FCSTD DOCUMENT  (FreeCAD 0.18R15684 (Git))
Label: pattern_test_knot4_path
License: All rights reserved
LicenseURL: http://en.wikipedia.org/wiki/All_rights_reserved
objects: Sketcher::SketchObject×244, Part::Feature×243, App::DocumentObjectGroup×2
note: 487 computed .brp shape members not serialized (recipe doc carries the construction recipe); baked Part::Feature solids carry a one-line shape summary decoded from their .brp

FEATURE [Part::Feature] path1691
  shape: bbox 0.3504 x 2.048 x 2e-07 mm, 0 faces, 0 solids (baked)
FEATURE [Part::Feature] path1691001
  shape: bbox 5.227 x 10.07 x 2e-07 mm, 0 faces, 0 solids (baked)
FEATURE [Part::Feature] path1691002
  shape: bbox 3.62 x 11.21 x 2e-07 mm, 0 faces, 0 solids (baked)
FEATURE [Part::Feature] path1691003
  shape: bbox 0.9578 x 6.153 x 2e-07 mm, 0 faces, 0 solids (baked)
FEATURE [Part::Feature] path1691004
  shape: bbox 2.257 x 12.25 x 2e-07 mm, 0 faces, 0 solids (baked)
FEATURE [Part::Feature] path1691005
  shape: bbox 7.072 x 2.907 x 2e-07 mm, 0 faces, 0 solids (baked)
FEATURE [Part::Feature] path1691006
  shape: bbox 2.023 x 11.54 x 2e-07 mm, 0 faces, 0 solids (baked)
FEATURE [Part::Feature] path1691007
  shape: bbox 7.186 x 8.882 x 2e-07 mm, 0 faces, 0 solids (baked)
FEATURE [Part::Feature] path1691008
  shape: bbox 1.074 x 1.58 x 2e-07 mm, 0 faces, 0 solids (baked)
FEATURE [Part::Feature] path1691009
  shape: bbox 0.9879 x 3.768 x 2e-07 mm, 0 faces, 0 solids (baked)
FEATURE [Part::Feature] path1691010
  shape: bbox 4.571 x 8.635 x 2e-07 mm, 0 faces, 0 solids (baked)
FEATURE [Part::Feature] path1691011
  shape: bbox 3.861 x 12.64 x 2e-07 mm, 0 faces, 0 solids (baked)
FEATURE [Part::Feature] path1691012
  shape: bbox 0.7387 x 5.6 x 2e-07 mm, 0 faces, 0 solids (baked)
FEATURE [Part::Feature] path1691013
  shape: bbox 3.309 x 14.24 x 2e-07 mm, 0 faces, 0 solids (baked)
FEATURE [Part::Feature] path1691014
  shape: bbox 6.225 x 2.806 x 2e-07 mm, 0 faces, 0 solids (baked)
FEATURE [Part::Feature] path1691015
  shape: bbox 1.988 x 12.93 x 2e-07 mm, 0 faces, 0 solids (baked)
FEATURE [Part::Feature] path1691016
  shape: bbox 6.325 x 7.842 x 2e-07 mm, 0 faces, 0 solids (baked)
FEATURE [Part::Feature] path1691017
  shape: bbox 1.621 x 2.832 x 2e-07 mm, 0 faces, 0 solids (baked)
FEATURE [Part::Feature] path1691018
  shape: bbox 1.588 x 5.097 x 2e-07 mm, 0 faces, 0 solids (baked)
FEATURE [Part::Feature] path1691019
  shape: bbox 3.926 x 7.273 x 2e-07 mm, 0 faces, 0 solids (baked)
FEATURE [Part::Feature] path1691020
  shape: bbox 4.039 x 13.86 x 2e-07 mm, 0 faces, 0 solids (baked)
FEATURE [Part::Feature] path1691021
  shape: bbox 0.5401 x 5.018 x 2e-07 mm, 0 faces, 0 solids (baked)
FEATURE [Part::Feature] path1691022
  shape: bbox 4.309 x 15.69 x 2e-07 mm, 0 faces, 0 solids (baked)
FEATURE [Part::Feature] path1691023
  shape: bbox 5.323 x 2.698 x 2e-07 mm, 0 faces, 0 solids (baked)
FEATURE [Part::Feature] path1691024
  shape: bbox 1.922 x 3.803 x 2e-07 mm, 0 faces, 0 solids (baked)
FEATURE [Part::Feature] path1691025
  shape: bbox 5.434 x 6.81 x 2e-07 mm, 0 faces, 0 solids (baked)
FEATURE [Part::Feature] path1691026
  shape: bbox 2.605 x 14.03 x 2e-07 mm, 0 faces, 0 solids (baked)
FEATURE [Part::Feature] path1691027
  shape: bbox 1.567 x 1.328 x 2e-07 mm, 0 faces, 0 solids (baked)
FEATURE [Part::Feature] path1691028
  shape: bbox 10.31 x 5.187 x 2e-07 mm, 0 faces, 0 solids (baked)
FEATURE [Part::Feature] path1691029
  shape: bbox 9.647 x 6.66 x 2e-07 mm, 0 faces, 0 solids (baked)
FEATURE [Part::Feature] path1691030
  shape: bbox 3.288 x 5.429 x 2e-07 mm, 0 faces, 0 solids (baked)
FEATURE [Part::Feature] path1691031
  shape: bbox 8.702 x 8.842 x 2e-07 mm, 0 faces, 0 solids (baked)
FEATURE [Part::Feature] path1691032
  shape: bbox 7.276 x 2.368 x 2e-07 mm, 0 faces, 0 solids (baked)
FEATURE [Part::Feature] path1691033
  shape: bbox 6.363 x 9.776 x 2e-07 mm, 0 faces, 0 solids (baked)
FEATURE [Part::Feature] path1691034
  shape: bbox 11.06 x 3.666 x 2e-07 mm, 0 faces, 0 solids (baked)
FEATURE [Part::Feature] path1691035
  shape: bbox 1.798 x 0.5737 x 2e-07 mm, 0 faces, 0 solids (baked)
FEATURE [Part::Feature] path1691036
  shape: bbox 3.13 x 2.234 x 2e-07 mm, 0 faces, 0 solids (baked)
FEATURE [Part::Feature] path1691037
  shape: bbox 8.964 x 4.497 x 2e-07 mm, 0 faces, 0 solids (baked)
FEATURE [Part::Feature] path1691038
  shape: bbox 10.73 x 7.659 x 2e-07 mm, 0 faces, 0 solids (baked)
FEATURE [Part::Feature] path1691039
  shape: bbox 3.078 x 4.836 x 2e-07 mm, 0 faces, 0 solids (baked)
FEATURE [Part::Feature] path1691040
  shape: bbox 10.67 x 9.895 x 2e-07 mm, 0 faces, 0 solids (baked)
FEATURE [Part::Feature] path1691041
  shape: bbox 6.563 x 1.898 x 2e-07 mm, 0 faces, 0 solids (baked)
FEATURE [Part::Feature] path1691042
  shape: bbox 7.893 x 10.29 x 2e-07 mm, 0 faces, 0 solids (baked)
FEATURE [Part::Feature] path1691043
  shape: bbox 9.755 x 3.159 x 2e-07 mm, 0 faces, 0 solids (baked)
FEATURE [Part::Feature] path1691044
  shape: bbox 2.994 x 1.224 x 2e-07 mm, 0 faces, 0 solids (baked)
FEATURE [Part::Feature] path1691045
  shape: bbox 4.409 x 2.869 x 2e-07 mm, 0 faces, 0 solids (baked)
FEATURE [Part::Feature] path1691046
  shape: bbox 7.616 x 3.823 x 2e-07 mm, 0 faces, 0 solids (baked)
FEATURE [Part::Feature] path1691047
  shape: bbox 11.63 x 8.524 x 2e-07 mm, 0 faces, 0 solids (baked)
FEATURE [Part::Feature] path1691048
  shape: bbox 2.836 x 4.236 x 2e-07 mm, 0 faces, 0 solids (baked)
FEATURE [Part::Feature] path1691049
  shape: bbox 12.27 x 10.71 x 2e-07 mm, 0 faces, 0 solids (baked)
FEATURE [Part::Feature] path1691050
  shape: bbox 5.802 x 1.397 x 2e-07 mm, 0 faces, 0 solids (baked)
FEATURE [Part::Feature] path1691051
  shape: bbox 3.83 x 1.807 x 2e-07 mm, 0 faces, 0 solids (baked)
FEATURE [Part::Feature] path1691052
  shape: bbox 8.427 x 2.641 x 2e-07 mm, 0 faces, 0 solids (baked)
FEATURE [Part::Feature] path1691053
  shape: bbox 9.259 x 10.56 x 2e-07 mm, 0 faces, 0 solids (baked)
FEATURE [Part::Feature] path1691054
  shape: bbox 2.053 x 0.14 x 2e-07 mm, 0 faces, 0 solids (baked)
FEATURE [Part::Feature] path1691055
  shape: bbox 10.87 x 3.857 x 2e-07 mm, 0 faces, 0 solids (baked)
FEATURE [Part::Feature] path1691056
  shape: bbox 11.6 x 1.97 x 2e-07 mm, 0 faces, 0 solids (baked)
FEATURE [Part::Feature] path1691057
  shape: bbox 5.851 x 2.085 x 2e-07 mm, 0 faces, 0 solids (baked)
FEATURE [Part::Feature] path1691058
  shape: bbox 12.33 x 2.079 x 2e-07 mm, 0 faces, 0 solids (baked)
FEATURE [Part::Feature] path1691059
  shape: bbox 3.992 x 6.473 x 2e-07 mm, 0 faces, 0 solids (baked)
FEATURE [Part::Feature] path1691060
  shape: bbox 11.13 x 3.76 x 2e-07 mm, 0 faces, 0 solids (baked)
FEATURE [Part::Feature] path1691061
  shape: bbox 9.944 x 5.853 x 2e-07 mm, 0 faces, 0 solids (baked)
FEATURE [Part::Feature] path1691062
  shape: bbox 1.723 x 0.8025 x 2e-07 mm, 0 faces, 0 solids (baked)
FEATURE [Part::Feature] path1691063
  shape: bbox 3.852 x 0.4329 x 2e-07 mm, 0 faces, 0 solids (baked)
FEATURE [Part::Feature] path1691064
  shape: bbox 9.373 x 3.39 x 2e-07 mm, 0 faces, 0 solids (baked)
FEATURE [Part::Feature] path1691065
  shape: bbox 13.06 x 2.031 x 2e-07 mm, 0 faces, 0 solids (baked)
FEATURE [Part::Feature] path1691066
  shape: bbox 5.344 x 1.781 x 2e-07 mm, 0 faces, 0 solids (baked)
FEATURE [Part::Feature] path1691067
  shape: bbox 14.47 x 2.375 x 2e-07 mm, 0 faces, 0 solids (baked)
FEATURE [Part::Feature] path1691068
  shape: bbox 3.759 x 5.66 x 2e-07 mm, 0 faces, 0 solids (baked)
FEATURE [Part::Feature] path1691069
  shape: bbox 12.68 x 3.785 x 2e-07 mm, 0 faces, 0 solids (baked)
FEATURE [Part::Feature] path1691070
  shape: bbox 8.781 x 5.094 x 2e-07 mm, 0 faces, 0 solids (baked)
FEATURE [Part::Feature] path1691071
  shape: bbox 3.044 x 1.138 x 2e-07 mm, 0 faces, 0 solids (baked)
FEATURE [Part::Feature] path1691072
  shape: bbox 5.268 x 0.8515 x 2e-07 mm, 0 faces, 0 solids (baked)
FEATURE [Part::Feature] path1691073
  shape: bbox 7.923 x 2.859 x 2e-07 mm, 0 faces, 0 solids (baked)
FEATURE [Part::Feature] path1691074
  shape: bbox 14.31 x 2.101 x 2e-07 mm, 0 faces, 0 solids (baked)
FEATURE [Part::Feature] path1691075
  shape: bbox 4.805 x 1.488 x 2e-07 mm, 0 faces, 0 solids (baked)
FEATURE [Part::Feature] path1691076
  shape: bbox 16.08 x 3.163 x 2e-07 mm, 0 faces, 0 solids (baked)
FEATURE [Part::Feature] path1691077
  shape: bbox 3.509 x 4.794 x 2e-07 mm, 0 faces, 0 solids (baked)
FEATURE [Part::Feature] path1691078
  shape: bbox 4.05 x 1.277 x 2e-07 mm, 0 faces, 0 solids (baked)
FEATURE [Part::Feature] path1691079
  shape: bbox 7.619 x 4.304 x 2e-07 mm, 0 faces, 0 solids (baked)
FEATURE [Part::Feature] path1691080
  shape: bbox 13.94 x 3.811 x 2e-07 mm, 0 faces, 0 solids (baked)
FEATURE [Part::Feature] path1691081
  shape: bbox 1.559 x 1.332 x 2e-07 mm, 0 faces, 0 solids (baked)
FEATURE [Part::Feature] path1691082
  shape: bbox 6.467 x 9.433 x 2e-07 mm, 0 faces, 0 solids (baked)
FEATURE [Part::Feature] path1691083
  shape: bbox 8.24 x 8.385 x 2e-07 mm, 0 faces, 0 solids (baked)
FEATURE [Part::Feature] path1691084
  shape: bbox 5.856 x 2.384 x 2e-07 mm, 0 faces, 0 solids (baked)
FEATURE [Part::Feature] path1691085
  shape: bbox 10.15 x 7.19 x 2e-07 mm, 0 faces, 0 solids (baked)
FEATURE [Part::Feature] path1691086
  shape: bbox 1.382 x 7.554 x 2e-07 mm, 0 faces, 0 solids (baked)
FEATURE [Part::Feature] path1691087
  shape: bbox 10.65 x 4.733 x 2e-07 mm, 0 faces, 0 solids (baked)
FEATURE [Part::Feature] path1691088
  shape: bbox 4.738 x 10.52 x 2e-07 mm, 0 faces, 0 solids (baked)
FEATURE [Part::Feature] path1691089
  shape: bbox 0.8897 x 1.671 x 2e-07 mm, 0 faces, 0 solids (baked)
FEATURE [Part::Feature] path1691090
  shape: bbox 2.702 x 2.728 x 2e-07 mm, 0 faces, 0 solids (baked)
FEATURE [Part::Feature] path1691091
  shape: bbox 5.533 x 8.223 x 2e-07 mm, 0 faces, 0 solids (baked)
FEATURE [Part::Feature] path1691092
  shape: bbox 9.397 x 9.277 x 2e-07 mm, 0 faces, 0 solids (baked)
FEATURE [Part::Feature] path1691093
  shape: bbox 5.241 x 2.269 x 2e-07 mm, 0 faces, 0 solids (baked)
FEATURE [Part::Feature] path1691094
  shape: bbox 11.46 x 8.969 x 2e-07 mm, 0 faces, 0 solids (baked)
FEATURE [Part::Feature] path1691095
  shape: bbox 1.062 x 6.767 x 2e-07 mm, 0 faces, 0 solids (baked)
FEATURE [Part::Feature] path1691096
  shape: bbox 11.4 x 6.16 x 2e-07 mm, 0 faces, 0 solids (baked)
FEATURE [Part::Feature] path1691097
  shape: bbox 4.178 x 9.267 x 2e-07 mm, 0 faces, 0 solids (baked)
FEATURE [Part::Feature] path1691098
  shape: bbox 1.74 x 2.734 x 2e-07 mm, 0 faces, 0 solids (baked)
FEATURE [Part::Feature] path1691099
  shape: bbox 3.534 x 3.887 x 2e-07 mm, 0 faces, 0 solids (baked)
FEATURE [Part::Feature] path1691100
  shape: bbox 4.691 x 7 x 2e-07 mm, 0 faces, 0 solids (baked)
FEATURE [Part::Feature] path1691101
  shape: bbox 10.39 x 10.01 x 2e-07 mm, 0 faces, 0 solids (baked)
FEATURE [Part::Feature] path1691102
  shape: bbox 4.616 x 2.124 x 2e-07 mm, 0 faces, 0 solids (baked)
FEATURE [Part::Feature] path1691103
  shape: bbox 12.38 x 10.45 x 2e-07 mm, 0 faces, 0 solids (baked)
FEATURE [Part::Feature] path1691104
  shape: bbox 0.7061 x 5.928 x 2e-07 mm, 0 faces, 0 solids (baked)
FEATURE [Part::Feature] path1691105
  shape: bbox 2.457 x 3.454 x 2e-07 mm, 0 faces, 0 solids (baked)
FEATURE [Part::Feature] path1691106
  shape: bbox 3.576 x 7.994 x 2e-07 mm, 0 faces, 0 solids (baked)
FEATURE [Part::Feature] path1691107
  shape: bbox 11.89 x 7.465 x 2e-07 mm, 0 faces, 0 solids (baked)
FEATURE [Part::Feature] path1691108
  shape: bbox 0.4326 x 2 x 2e-07 mm, 0 faces, 0 solids (baked)
FEATURE [Part::Feature] path1691109
  shape: bbox 2.613 x 11.26 x 2e-07 mm, 0 faces, 0 solids (baked)
FEATURE [Part::Feature] path1691110
  shape: bbox 1.547 x 11.7 x 2e-07 mm, 0 faces, 0 solids (baked)
FEATURE [Part::Feature] path1691111
  shape: bbox 3.166 x 5.368 x 2e-07 mm, 0 faces, 0 solids (baked)
FEATURE [Part::Feature] path1691112
  shape: bbox 3.608 x 12.03 x 2e-07 mm, 0 faces, 0 solids (baked)
FEATURE [Part::Feature] path1691113
  shape: bbox 5.654 x 5.019 x 2e-07 mm, 0 faces, 0 solids (baked)
FEATURE [Part::Feature] path1691114
  shape: bbox 5.507 x 10.23 x 2e-07 mm, 0 faces, 0 solids (baked)
FEATURE [Part::Feature] path1691115
  shape: bbox 4.502 x 10.81 x 2e-07 mm, 0 faces, 0 solids (baked)
FEATURE [Part::Feature] path1691116
  shape: bbox 0.4953 x 1.824 x 2e-07 mm, 0 faces, 0 solids (baked)
FEATURE [Part::Feature] path1691117
  shape: bbox 0.6326 x 3.804 x 2e-07 mm, 0 faces, 0 solids (baked)
FEATURE [Part::Feature] path1691118
  shape: bbox 2.308 x 9.728 x 2e-07 mm, 0 faces, 0 solids (baked)
FEATURE [Part::Feature] path1691119
  shape: bbox 1.838 x 13.16 x 2e-07 mm, 0 faces, 0 solids (baked)
FEATURE [Part::Feature] path1691120
  shape: bbox 2.759 x 4.923 x 2e-07 mm, 0 faces, 0 solids (baked)
FEATURE [Part::Feature] path1691121
  shape: bbox 4.121 x 14.25 x 2e-07 mm, 0 faces, 0 solids (baked)
FEATURE [Part::Feature] path1691122
  shape: bbox 4.903 x 4.653 x 2e-07 mm, 0 faces, 0 solids (baked)
FEATURE [Part::Feature] path1691123
  shape: bbox 5.585 x 11.85 x 2e-07 mm, 0 faces, 0 solids (baked)
FEATURE [Part::Feature] path1691124
  shape: bbox 3.857 x 9.555 x 2e-07 mm, 0 faces, 0 solids (baked)
FEATURE [Part::Feature] path1691125
  shape: bbox 0.6126 x 3.18 x 2e-07 mm, 0 faces, 0 solids (baked)
FEATURE [Part::Feature] path1691126
  shape: bbox 0.8239 x 5.237 x 2e-07 mm, 0 faces, 0 solids (baked)
FEATURE [Part::Feature] path1691127
  shape: bbox 1.948 x 8.238 x 2e-07 mm, 0 faces, 0 solids (baked)
FEATURE [Part::Feature] path1691128
  shape: bbox 2.112 x 14.4 x 2e-07 mm, 0 faces, 0 solids (baked)
FEATURE [Part::Feature] path1691129
  shape: bbox 2.359 x 4.445 x 2e-07 mm, 0 faces, 0 solids (baked)
FEATURE [Part::Feature] path1691130
  shape: bbox 4.537 x 15.95 x 2e-07 mm, 0 faces, 0 solids (baked)
FEATURE [Part::Feature] path1691131
  shape: bbox 4.102 x 4.262 x 2e-07 mm, 0 faces, 0 solids (baked)
FEATURE [Part::Feature] path1691132
  shape: bbox 0.6865 x 4.196 x 2e-07 mm, 0 faces, 0 solids (baked)
FEATURE [Part::Feature] path1691133
  shape: bbox 3.179 x 8.287 x 2e-07 mm, 0 faces, 0 solids (baked)
FEATURE [Part::Feature] path1691134
  shape: bbox 5.662 x 13.21 x 2e-07 mm, 0 faces, 0 solids (baked)
FEATURE [Part::Feature] path1691135
  shape: bbox 1.05 x 1.756 x 2e-07 mm, 0 faces, 0 solids (baked)
FEATURE [Part::Feature] path1691136
  shape: bbox 8.272 x 7.856 x 2e-07 mm, 0 faces, 0 solids (baked)
FEATURE [Part::Feature] path1691137
  shape: bbox 6.96 x 9.524 x 2e-07 mm, 0 faces, 0 solids (baked)
FEATURE [Part::Feature] path1691138
  shape: bbox 1.375 x 6.119 x 2e-07 mm, 0 faces, 0 solids (baked)
FEATURE [Part::Feature] path1691139
  shape: bbox 5.496 x 11.16 x 2e-07 mm, 0 faces, 0 solids (baked)
FEATURE [Part::Feature] path1691140
  shape: bbox 7.613 x 1.186 x 2e-07 mm, 0 faces, 0 solids (baked)
FEATURE [Part::Feature] path1691141
  shape: bbox 2.932 x 11.23 x 2e-07 mm, 0 faces, 0 solids (baked)
FEATURE [Part::Feature] path1691142
  shape: bbox 9.689 x 6.196 x 2e-07 mm, 0 faces, 0 solids (baked)
FEATURE [Part::Feature] path1691143
  shape: bbox 1.508 x 1.163 x 2e-07 mm, 0 faces, 0 solids (baked)
FEATURE [Part::Feature] path1691144
  shape: bbox 2.237 x 3.114 x 2e-07 mm, 0 faces, 0 solids (baked)
FEATURE [Part::Feature] path1691145
  shape: bbox 7.24 x 6.674 x 2e-07 mm, 0 faces, 0 solids (baked)
FEATURE [Part::Feature] path1691146
  shape: bbox 7.65 x 10.81 x 2e-07 mm, 0 faces, 0 solids (baked)
FEATURE [Part::Feature] path1691147
  shape: bbox 1.364 x 5.504 x 2e-07 mm, 0 faces, 0 solids (baked)
FEATURE [Part::Feature] path1691148
  shape: bbox 7.043 x 12.73 x 2e-07 mm, 0 faces, 0 solids (baked)
FEATURE [Part::Feature] path1691149
  shape: bbox 6.778 x 1.178 x 2e-07 mm, 0 faces, 0 solids (baked)
FEATURE [Part::Feature] path1691150
  shape: bbox 4.221 x 12.21 x 2e-07 mm, 0 faces, 0 solids (baked)
FEATURE [Part::Feature] path1691151
  shape: bbox 8.532 x 5.472 x 2e-07 mm, 0 faces, 0 solids (baked)
FEATURE [Part::Feature] path1691152
  shape: bbox 2.419 x 2.18 x 2e-07 mm, 0 faces, 0 solids (baked)
FEATURE [Part::Feature] path1691153
  shape: bbox 3.244 x 4.127 x 2e-07 mm, 0 faces, 0 solids (baked)
FEATURE [Part::Feature] path1691154
  shape: bbox 6.18 x 5.581 x 2e-07 mm, 0 faces, 0 solids (baked)
FEATURE [Part::Feature] path1691155
  shape: bbox 8.212 x 11.9 x 2e-07 mm, 0 faces, 0 solids (baked)
FEATURE [Part::Feature] path1691156
  shape: bbox 1.324 x 4.873 x 2e-07 mm, 0 faces, 0 solids (baked)
FEATURE [Part::Feature] path1691157
  shape: bbox 8.367 x 13.8 x 2e-07 mm, 0 faces, 0 solids (baked)
FEATURE [Part::Feature] path1691158
  shape: bbox 5.89 x 1.18 x 2e-07 mm, 0 faces, 0 solids (baked)
FEATURE [Part::Feature] path1691159
  shape: bbox 3.01 x 3.007 x 2e-07 mm, 0 faces, 0 solids (baked)
FEATURE [Part::Feature] path1691160
  shape: bbox 7.35 x 4.767 x 2e-07 mm, 0 faces, 0 solids (baked)
FEATURE [Part::Feature] path1691161
  shape: bbox 5.432 x 12.91 x 2e-07 mm, 0 faces, 0 solids (baked)
FEATURE [Part::Feature] path1691162
  shape: bbox 1.901 x 0.7651 x 2e-07 mm, 0 faces, 0 solids (baked)
FEATURE [Part::Feature] path1691163
  shape: bbox 11.22 x 2.933 x 2e-07 mm, 0 faces, 0 solids (baked)
FEATURE [Part::Feature] path1691164
  shape: bbox 11.48 x 3.19 x 2e-07 mm, 0 faces, 0 solids (baked)
FEATURE [Part::Feature] path1691165
  shape: bbox 4.779 x 4.084 x 2e-07 mm, 0 faces, 0 solids (baked)
FEATURE [Part::Feature] path1691166
  shape: bbox 11.18 x 5.58 x 2e-07 mm, 0 faces, 0 solids (baked)
FEATURE [Part::Feature] path1691167
  shape: bbox 5.988 x 4.615 x 2e-07 mm, 0 faces, 0 solids (baked)
FEATURE [Part::Feature] path1691168
  shape: bbox 9.109 x 7.176 x 2e-07 mm, 0 faces, 0 solids (baked)
FEATURE [Part::Feature] path1691169
  shape: bbox 11.3 x 3.072 x 2e-07 mm, 0 faces, 0 solids (baked)
FEATURE [Part::Feature] path1691170
  shape: bbox 1.882 x 0.1704 x 2e-07 mm, 0 faces, 0 solids (baked)
FEATURE [Part::Feature] path1691171
  shape: bbox 3.668 x 1.129 x 2e-07 mm, 0 faces, 0 solids (baked)
FEATURE [Part::Feature] path1691172
  shape: bbox 9.716 x 2.495 x 2e-07 mm, 0 faces, 0 solids (baked)
FEATURE [Part::Feature] path1691173
  shape: bbox 12.87 x 3.753 x 2e-07 mm, 0 faces, 0 solids (baked)
FEATURE [Part::Feature] path1691174
  shape: bbox 4.405 x 3.594 x 2e-07 mm, 0 faces, 0 solids (baked)
FEATURE [Part::Feature] path1691175
  shape: bbox 13.4 x 6.275 x 2e-07 mm, 0 faces, 0 solids (baked)
FEATURE [Part::Feature] path1691176
  shape: bbox 5.49 x 3.953 x 2e-07 mm, 0 faces, 0 solids (baked)
FEATURE [Part::Feature] path1691177
  shape: bbox 10.74 x 7.298 x 2e-07 mm, 0 faces, 0 solids (baked)
FEATURE [Part::Feature] path1691178
  shape: bbox 9.987 x 2.571 x 2e-07 mm, 0 faces, 0 solids (baked)
FEATURE [Part::Feature] path1691179
  shape: bbox 3.24 x 0.2046 x 2e-07 mm, 0 faces, 0 solids (baked)
FEATURE [Part::Feature] path1691180
  shape: bbox 5.084 x 1.492 x 2e-07 mm, 0 faces, 0 solids (baked)
FEATURE [Part::Feature] path1691181
  shape: bbox 8.235 x 2.06 x 2e-07 mm, 0 faces, 0 solids (baked)
FEATURE [Part::Feature] path1691182
  shape: bbox 14.05 x 4.261 x 2e-07 mm, 0 faces, 0 solids (baked)
FEATURE [Part::Feature] path1691183
  shape: bbox 3.996 x 3.108 x 2e-07 mm, 0 faces, 0 solids (baked)
FEATURE [Part::Feature] path1691184
  shape: bbox 15.13 x 6.831 x 2e-07 mm, 0 faces, 0 solids (baked)
FEATURE [Part::Feature] path1691185
  shape: bbox 4.957 x 3.245 x 2e-07 mm, 0 faces, 0 solids (baked)
FEATURE [Part::Feature] path1691186
  shape: bbox 4.241 x 0.4552 x 2e-07 mm, 0 faces, 0 solids (baked)
FEATURE [Part::Feature] path1691187
  shape: bbox 8.661 x 2.04 x 2e-07 mm, 0 faces, 0 solids (baked)
FEATURE [Part::Feature] path1691188
  shape: bbox 12.13 x 7.421 x 2e-07 mm, 0 faces, 0 solids (baked)
FEATURE [Part::Feature] path1691189
  shape: bbox 1.919 x 0.7232 x 2e-07 mm, 0 faces, 0 solids (baked)
FEATURE [Part::Feature] path1691190
  shape: bbox 9.057 x 6.83 x 2e-07 mm, 0 faces, 0 solids (baked)
FEATURE [Part::Feature] path1691191
  shape: bbox 10.51 x 5.371 x 2e-07 mm, 0 faces, 0 solids (baked)
FEATURE [Part::Feature] path1691192
  shape: bbox 6.218 x 0.5371 x 2e-07 mm, 0 faces, 0 solids (baked)
FEATURE [Part::Feature] path1691193
  shape: bbox 11.86 x 3.621 x 2e-07 mm, 0 faces, 0 solids (baked)
FEATURE [Part::Feature] path1691194
  shape: bbox 1.984 x 7.452 x 2e-07 mm, 0 faces, 0 solids (baked)
FEATURE [Part::Feature] path1691195
  shape: bbox 11.53 x 1.358 x 2e-07 mm, 0 faces, 0 solids (baked)
FEATURE [Part::Feature] path1691196
  shape: bbox 7.633 x 8.579 x 2e-07 mm, 0 faces, 0 solids (baked)
FEATURE [Part::Feature] path1691197
  shape: bbox 1.393 x 1.309 x 2e-07 mm, 0 faces, 0 solids (baked)
FEATURE [Part::Feature] path1691198
  shape: bbox 3.469 x 1.657 x 2e-07 mm, 0 faces, 0 solids (baked)
FEATURE [Part::Feature] path1691199
  shape: bbox 7.733 x 6.015 x 2e-07 mm, 0 faces, 0 solids (baked)
FEATURE [Part::Feature] path1691200
  shape: bbox 11.89 x 5.845 x 2e-07 mm, 0 faces, 0 solids (baked)
FEATURE [Part::Feature] path1691201
  shape: bbox 5.624 x 0.4799 x 2e-07 mm, 0 faces, 0 solids (baked)
FEATURE [Part::Feature] path1691202
  shape: bbox 13.66 x 4.892 x 2e-07 mm, 0 faces, 0 solids (baked)
FEATURE [Part::Feature] path1691203
  shape: bbox 1.795 x 6.598 x 2e-07 mm, 0 faces, 0 solids (baked)
FEATURE [Part::Feature] path1691204
  shape: bbox 12.72 x 2.425 x 2e-07 mm, 0 faces, 0 solids (baked)
FEATURE [Part::Feature] path1691205
  shape: bbox 6.739 x 7.552 x 2e-07 mm, 0 faces, 0 solids (baked)
FEATURE [Part::Feature] path1691206
  shape: bbox 2.544 x 2.047 x 2e-07 mm, 0 faces, 0 solids (baked)
FEATURE [Part::Feature] path1691207
  shape: bbox 4.648 x 2.477 x 2e-07 mm, 0 faces, 0 solids (baked)
FEATURE [Part::Feature] path1691208
  shape: bbox 6.491 x 5.155 x 2e-07 mm, 0 faces, 0 solids (baked)
FEATURE [Part::Feature] path1691209
  shape: bbox 13.06 x 6.22 x 2e-07 mm, 0 faces, 0 solids (baked)
FEATURE [Part::Feature] path1691210
  shape: bbox 5.007 x 0.4917 x 2e-07 mm, 0 faces, 0 solids (baked)
FEATURE [Part::Feature] path1691211
  shape: bbox 14.93 x 6.051 x 2e-07 mm, 0 faces, 0 solids (baked)
FEATURE [Part::Feature] path1691212
  shape: bbox 1.829 x 5.689 x 2e-07 mm, 0 faces, 0 solids (baked)
FEATURE [Part::Feature] path1691213
  shape: bbox 3.455 x 2.499 x 2e-07 mm, 0 faces, 0 solids (baked)
FEATURE [Part::Feature] path1691214
  shape: bbox 5.859 x 6.497 x 2e-07 mm, 0 faces, 0 solids (baked)
FEATURE [Part::Feature] path1691215
  shape: bbox 13.62 x 3.465 x 2e-07 mm, 0 faces, 0 solids (baked)
FEATURE [Part::Feature] path1691216
  shape: bbox 1.064 x 1.757 x 2e-07 mm, 0 faces, 0 solids (baked)
FEATURE [Part::Feature] path1691217
  shape: bbox 4.06 x 10.91 x 2e-07 mm, 0 faces, 0 solids (baked)
FEATURE [Part::Feature] path1691218
  shape: bbox 4.785 x 10.75 x 2e-07 mm, 0 faces, 0 solids (baked)
FEATURE [Part::Feature] path1691219
  shape: bbox 4.839 x 4.086 x 2e-07 mm, 0 faces, 0 solids (baked)
FEATURE [Part::Feature] path1691220
  shape: bbox 7.23 x 10.03 x 2e-07 mm, 0 faces, 0 solids (baked)
FEATURE [Part::Feature] path1691221
  shape: bbox 3.394 x 6.779 x 2e-07 mm, 0 faces, 0 solids (baked)
FEATURE [Part::Feature] path1691222
  shape: bbox 8.619 x 7.822 x 2e-07 mm, 0 faces, 0 solids (baked)
FEATURE [Part::Feature] path1691223
  shape: bbox 2.678 x 11.33 x 2e-07 mm, 0 faces, 0 solids (baked)
FEATURE [Part::Feature] path1691224
  shape: bbox 0.2165 x 1.889 x 2e-07 mm, 0 faces, 0 solids (baked)
FEATURE [Part::Feature] path1691225
  shape: bbox 1.71 x 3.444 x 2e-07 mm, 0 faces, 0 solids (baked)
FEATURE [Part::Feature] path1691226
  shape: bbox 3.504 x 9.461 x 2e-07 mm, 0 faces, 0 solids (baked)
FEATURE [Part::Feature] path1691227
  shape: bbox 5.592 x 12 x 2e-07 mm, 0 faces, 0 solids (baked)
FEATURE [Part::Feature] path1691228
  shape: bbox 4.287 x 3.79 x 2e-07 mm, 0 faces, 0 solids (baked)
FEATURE [Part::Feature] path1691229
  shape: bbox 8.111 x 12.15 x 2e-07 mm, 0 faces, 0 solids (baked)
FEATURE [Part::Feature] path1691230
  shape: bbox 2.828 x 6.167 x 2e-07 mm, 0 faces, 0 solids (baked)
FEATURE [Part::Feature] path1691231
  shape: bbox 8.888 x 9.419 x 2e-07 mm, 0 faces, 0 solids (baked)
FEATURE [Part::Feature] path1691232
  shape: bbox 2.247 x 9.998 x 2e-07 mm, 0 faces, 0 solids (baked)
FEATURE [Part::Feature] path1691233
  shape: bbox 0.632 x 3.198 x 2e-07 mm, 0 faces, 0 solids (baked)
FEATURE [Part::Feature] path1691234
  shape: bbox 2.132 x 4.808 x 2e-07 mm, 0 faces, 0 solids (baked)
FEATURE [Part::Feature] path1691235
  shape: bbox 2.952 x 8.028 x 2e-07 mm, 0 faces, 0 solids (baked)
FEATURE [Part::Feature] path1691236
  shape: bbox 6.302 x 13.05 x 2e-07 mm, 0 faces, 0 solids (baked)
FEATURE [Part::Feature] path1691237
  shape: bbox 3.733 x 3.46 x 2e-07 mm, 0 faces, 0 solids (baked)
FEATURE [Part::Feature] path1691238
  shape: bbox 8.822 x 13.83 x 2e-07 mm, 0 faces, 0 solids (baked)
FEATURE [Part::Feature] path1691239
  shape: bbox 2.226 x 5.512 x 2e-07 mm, 0 faces, 0 solids (baked)
FEATURE [Part::Feature] path1691240
  shape: bbox 1.056 x 4.14 x 2e-07 mm, 0 faces, 0 solids (baked)
FEATURE [Part::Feature] path1691241
  shape: bbox 1.813 x 8.651 x 2e-07 mm, 0 faces, 0 solids (baked)
FEATURE [Part::Feature] path1691242
  shape: bbox 9.06 x 10.82 x 2e-07 mm, 0 faces, 0 solids (baked)
FEATURE [Sketcher::SketchObject] Sketch
  sketch-geometry (1):
    g0: BSplineCurve PolesCount=4 KnotsCount=2 Degree=3 IsPeriodic=0
FEATURE [Sketcher::SketchObject] Sketch001
  sketch-geometry (1):
    g0: BSplineCurve PolesCount=4 KnotsCount=2 Degree=3 IsPeriodic=0
FEATURE [Sketcher::SketchObject] Sketch002
  sketch-geometry (2):
    g0: BSplineCurve PolesCount=4 KnotsCount=2 Degree=3 IsPeriodic=0
    g1: BSplineCurve PolesCount=4 KnotsCount=2 Degree=3 IsPeriodic=0
  constraints (1):
    c: Coincident(g0,g1)
FEATURE [Sketcher::SketchObject] Sketch003
  sketch-geometry (3):
    g0: BSplineCurve PolesCount=4 KnotsCount=2 Degree=3 IsPeriodic=0
    g1: BSplineCurve PolesCount=4 KnotsCount=2 Degree=3 IsPeriodic=0
    g2: BSplineCurve PolesCount=4 KnotsCount=2 Degree=3 IsPeriodic=0
  constraints (2):
    c: Coincident(g0,g1)
    c: Coincident(g1,g2)
FEATURE [Sketcher::SketchObject] Sketch004
  sketch-geometry (1):
    g0: BSplineCurve PolesCount=4 KnotsCount=2 Degree=3 IsPeriodic=0
FEATURE [Sketcher::SketchObject] Sketch005
  sketch-geometry (3):
    g0: BSplineCurve PolesCount=4 KnotsCount=2 Degree=3 IsPeriodic=0
    g1: BSplineCurve PolesCount=4 KnotsCount=2 Degree=3 IsPeriodic=0
    g2: BSplineCurve PolesCount=4 KnotsCount=2 Degree=3 IsPeriodic=0
  constraints (2):
    c: Coincident(g0,g1)
    c: Coincident(g1,g2)
FEATURE [Sketcher::SketchObject] Sketch006
  sketch-geometry (1):
    g0: BSplineCurve PolesCount=4 KnotsCount=2 Degree=3 IsPeriodic=0
FEATURE [Sketcher::SketchObject] Sketch007
  sketch-geometry (3):
    g0: BSplineCurve PolesCount=4 KnotsCount=2 Degree=3 IsPeriodic=0
    g1: BSplineCurve PolesCount=4 KnotsCount=2 Degree=3 IsPeriodic=0
    g2: BSplineCurve PolesCount=4 KnotsCount=2 Degree=3 IsPeriodic=0
  constraints (2):
    c: Coincident(g0,g1)
    c: Coincident(g1,g2)
FEATURE [Sketcher::SketchObject] Sketch008
  sketch-geometry (3):
    g0: BSplineCurve PolesCount=4 KnotsCount=2 Degree=3 IsPeriodic=0
    g1: BSplineCurve PolesCount=4 KnotsCount=2 Degree=3 IsPeriodic=0
    g2: BSplineCurve PolesCount=4 KnotsCount=2 Degree=3 IsPeriodic=0
  constraints (2):
    c: Coincident(g0,g1)
    c: Coincident(g1,g2)
FEATURE [Sketcher::SketchObject] Sketch009
  sketch-geometry (1):
    g0: BSplineCurve PolesCount=4 KnotsCount=2 Degree=3 IsPeriodic=0
FEATURE [Sketcher::SketchObject] Sketch010
  sketch-geometry (3):
    g0: BSplineCurve PolesCount=4 KnotsCount=2 Degree=3 IsPeriodic=0
    g1: BSplineCurve PolesCount=4 KnotsCount=2 Degree=3 IsPeriodic=0
    g2: BSplineCurve PolesCount=4 KnotsCount=2 Degree=3 IsPeriodic=0
  constraints (2):
    c: Coincident(g0,g1)
    c: Coincident(g1,g2)
FEATURE [Sketcher::SketchObject] Sketch011
  sketch-geometry (1):
    g0: BSplineCurve PolesCount=4 KnotsCount=2 Degree=3 IsPeriodic=0
FEATURE [Sketcher::SketchObject] Sketch012
  sketch-geometry (3):
    g0: BSplineCurve PolesCount=4 KnotsCount=2 Degree=3 IsPeriodic=0
    g1: BSplineCurve PolesCount=4 KnotsCount=2 Degree=3 IsPeriodic=0
    g2: BSplineCurve PolesCount=4 KnotsCount=2 Degree=3 IsPeriodic=0
  constraints (2):
    c: Coincident(g0,g1)
    c: Coincident(g1,g2)
FEATURE [Sketcher::SketchObject] Sketch013
  sketch-geometry (2):
    g0: BSplineCurve PolesCount=4 KnotsCount=2 Degree=3 IsPeriodic=0
    g1: BSplineCurve PolesCount=4 KnotsCount=2 Degree=3 IsPeriodic=0
  constraints (1):
    c: Coincident(g0,g1)
FEATURE [Sketcher::SketchObject] Sketch014
  sketch-geometry (1):
    g0: BSplineCurve PolesCount=4 KnotsCount=2 Degree=3 IsPeriodic=0
FEATURE [Sketcher::SketchObject] Sketch015
  sketch-geometry (2):
    g0: BSplineCurve PolesCount=4 KnotsCount=2 Degree=3 IsPeriodic=0
    g1: BSplineCurve PolesCount=4 KnotsCount=2 Degree=3 IsPeriodic=0
  constraints (1):
    c: Coincident(g0,g1)
FEATURE [Sketcher::SketchObject] Sketch016
  sketch-geometry (1):
    g0: BSplineCurve PolesCount=4 KnotsCount=2 Degree=3 IsPeriodic=0
FEATURE [Sketcher::SketchObject] Sketch017
  sketch-geometry (2):
    g0: BSplineCurve PolesCount=4 KnotsCount=2 Degree=3 IsPeriodic=0
    g1: BSplineCurve PolesCount=4 KnotsCount=2 Degree=3 IsPeriodic=0
  constraints (1):
    c: Coincident(g0,g1)
FEATURE [Sketcher::SketchObject] Sketch018
  sketch-geometry (3):
    g0: BSplineCurve PolesCount=4 KnotsCount=2 Degree=3 IsPeriodic=0
    g1: BSplineCurve PolesCount=4 KnotsCount=2 Degree=3 IsPeriodic=0
    g2: BSplineCurve PolesCount=4 KnotsCount=2 Degree=3 IsPeriodic=0
  constraints (2):
    c: Coincident(g0,g1)
    c: Coincident(g1,g2)
FEATURE [Sketcher::SketchObject] Sketch019
  sketch-geometry (1):
    g0: BSplineCurve PolesCount=4 KnotsCount=2 Degree=3 IsPeriodic=0
FEATURE [Sketcher::SketchObject] Sketch020
  sketch-geometry (3):
    g0: BSplineCurve PolesCount=4 KnotsCount=2 Degree=3 IsPeriodic=0
    g1: BSplineCurve PolesCount=4 KnotsCount=2 Degree=3 IsPeriodic=0
    g2: BSplineCurve PolesCount=4 KnotsCount=2 Degree=3 IsPeriodic=0
  constraints (2):
    c: Coincident(g0,g1)
    c: Coincident(g1,g2)
FEATURE [Sketcher::SketchObject] Sketch021
  sketch-geometry (1):
    g0: BSplineCurve PolesCount=4 KnotsCount=2 Degree=3 IsPeriodic=0
FEATURE [Sketcher::SketchObject] Sketch022
  sketch-geometry (1):
    g0: BSplineCurve PolesCount=4 KnotsCount=2 Degree=3 IsPeriodic=0
FEATURE [Sketcher::SketchObject] Sketch023
  sketch-geometry (1):
    g0: BSplineCurve PolesCount=4 KnotsCount=2 Degree=3 IsPeriodic=0
FEATURE [Sketcher::SketchObject] Sketch024
  sketch-geometry (1):
    g0: BSplineCurve PolesCount=4 KnotsCount=2 Degree=3 IsPeriodic=0
FEATURE [Sketcher::SketchObject] Sketch025
  sketch-geometry (2):
    g0: BSplineCurve PolesCount=4 KnotsCount=2 Degree=3 IsPeriodic=0
    g1: BSplineCurve PolesCount=4 KnotsCount=2 Degree=3 IsPeriodic=0
  constraints (1):
    c: Coincident(g0,g1)
FEATURE [Sketcher::SketchObject] Sketch026
  sketch-geometry (3):
    g0: BSplineCurve PolesCount=4 KnotsCount=2 Degree=3 IsPeriodic=0
    g1: BSplineCurve PolesCount=4 KnotsCount=2 Degree=3 IsPeriodic=0
    g2: BSplineCurve PolesCount=4 KnotsCount=2 Degree=3 IsPeriodic=0
  constraints (2):
    c: Coincident(g0,g1)
    c: Coincident(g1,g2)
FEATURE [Sketcher::SketchObject] Sketch027
  sketch-geometry (3):
    g0: BSplineCurve PolesCount=4 KnotsCount=2 Degree=3 IsPeriodic=0
    g1: BSplineCurve PolesCount=4 KnotsCount=2 Degree=3 IsPeriodic=0
    g2: BSplineCurve PolesCount=4 KnotsCount=2 Degree=3 IsPeriodic=0
  constraints (2):
    c: Coincident(g0,g1)
    c: Coincident(g1,g2)
FEATURE [Sketcher::SketchObject] Sketch028
  sketch-geometry (2):
    g0: BSplineCurve PolesCount=4 KnotsCount=2 Degree=3 IsPeriodic=0
    g1: BSplineCurve PolesCount=4 KnotsCount=2 Degree=3 IsPeriodic=0
  constraints (1):
    c: Coincident(g0,g1)
FEATURE [Sketcher::SketchObject] Sketch029
  sketch-geometry (3):
    g0: BSplineCurve PolesCount=4 KnotsCount=2 Degree=3 IsPeriodic=0
    g1: BSplineCurve PolesCount=4 KnotsCount=2 Degree=3 IsPeriodic=0
    g2: BSplineCurve PolesCount=4 KnotsCount=2 Degree=3 IsPeriodic=0
  constraints (2):
    c: Coincident(g0,g1)
    c: Coincident(g1,g2)
FEATURE [Sketcher::SketchObject] Sketch030
  sketch-geometry (1):
    g0: BSplineCurve PolesCount=4 KnotsCount=2 Degree=3 IsPeriodic=0
FEATURE [Sketcher::SketchObject] Sketch031
  sketch-geometry (3):
    g0: BSplineCurve PolesCount=4 KnotsCount=2 Degree=3 IsPeriodic=0
    g1: BSplineCurve PolesCount=4 KnotsCount=2 Degree=3 IsPeriodic=0
    g2: BSplineCurve PolesCount=4 KnotsCount=2 Degree=3 IsPeriodic=0
  constraints (2):
    c: Coincident(g0,g1)
    c: Coincident(g1,g2)
FEATURE [Sketcher::SketchObject] Sketch032
  sketch-geometry (1):
    g0: BSplineCurve PolesCount=4 KnotsCount=2 Degree=3 IsPeriodic=0
FEATURE [Sketcher::SketchObject] Sketch033
  sketch-geometry (1):
    g0: BSplineCurve PolesCount=4 KnotsCount=2 Degree=3 IsPeriodic=0
FEATURE [Sketcher::SketchObject] Sketch034
  sketch-geometry (2):
    g0: BSplineCurve PolesCount=4 KnotsCount=2 Degree=3 IsPeriodic=0
    g1: BSplineCurve PolesCount=4 KnotsCount=2 Degree=3 IsPeriodic=0
  constraints (1):
    c: Coincident(g0,g1)
FEATURE [Sketcher::SketchObject] Sketch035
  sketch-geometry (1):
    g0: BSplineCurve PolesCount=4 KnotsCount=2 Degree=3 IsPeriodic=0
FEATURE [Sketcher::SketchObject] Sketch036
  sketch-geometry (3):
    g0: BSplineCurve PolesCount=4 KnotsCount=2 Degree=3 IsPeriodic=0
    g1: BSplineCurve PolesCount=4 KnotsCount=2 Degree=3 IsPeriodic=0
    g2: BSplineCurve PolesCount=4 KnotsCount=2 Degree=3 IsPeriodic=0
  constraints (2):
    c: Coincident(g0,g1)
    c: Coincident(g1,g2)
FEATURE [Sketcher::SketchObject] Sketch037
  sketch-geometry (1):
    g0: BSplineCurve PolesCount=4 KnotsCount=2 Degree=3 IsPeriodic=0
FEATURE [Sketcher::SketchObject] Sketch038
  sketch-geometry (3):
    g0: BSplineCurve PolesCount=4 KnotsCount=2 Degree=3 IsPeriodic=0
    g1: BSplineCurve PolesCount=4 KnotsCount=2 Degree=3 IsPeriodic=0
    g2: BSplineCurve PolesCount=4 KnotsCount=2 Degree=3 IsPeriodic=0
  constraints (2):
    c: Coincident(g0,g1)
    c: Coincident(g1,g2)
FEATURE [Sketcher::SketchObject] Sketch039
  sketch-geometry (2):
    g0: BSplineCurve PolesCount=4 KnotsCount=2 Degree=3 IsPeriodic=0
    g1: BSplineCurve PolesCount=4 KnotsCount=2 Degree=3 IsPeriodic=0
  constraints (1):
    c: Coincident(g0,g1)
FEATURE [Sketcher::SketchObject] Sketch040
  sketch-geometry (1):
    g0: BSplineCurve PolesCount=4 KnotsCount=2 Degree=3 IsPeriodic=0
FEATURE [Sketcher::SketchObject] Sketch041
  sketch-geometry (1):
    g0: BSplineCurve PolesCount=4 KnotsCount=2 Degree=3 IsPeriodic=0
FEATURE [Sketcher::SketchObject] Sketch042
  sketch-geometry (2):
    g0: BSplineCurve PolesCount=4 KnotsCount=2 Degree=3 IsPeriodic=0
    g1: BSplineCurve PolesCount=4 KnotsCount=2 Degree=3 IsPeriodic=0
  constraints (1):
    c: Coincident(g0,g1)
FEATURE [Sketcher::SketchObject] Sketch043
  sketch-geometry (3):
    g0: BSplineCurve PolesCount=4 KnotsCount=2 Degree=3 IsPeriodic=0
    g1: BSplineCurve PolesCount=4 KnotsCount=2 Degree=3 IsPeriodic=0
    g2: BSplineCurve PolesCount=4 KnotsCount=2 Degree=3 IsPeriodic=0
  constraints (2):
    c: Coincident(g0,g1)
    c: Coincident(g1,g2)
FEATURE [Sketcher::SketchObject] Sketch044
  sketch-geometry (3):
    g0: BSplineCurve PolesCount=4 KnotsCount=2 Degree=3 IsPeriodic=0
    g1: BSplineCurve PolesCount=4 KnotsCount=2 Degree=3 IsPeriodic=0
    g2: BSplineCurve PolesCount=4 KnotsCount=2 Degree=3 IsPeriodic=0
  constraints (2):
    c: Coincident(g0,g1)
    c: Coincident(g1,g2)
FEATURE [Sketcher::SketchObject] Sketch045
  sketch-geometry (3):
    g0: BSplineCurve PolesCount=4 KnotsCount=2 Degree=3 IsPeriodic=0
    g1: BSplineCurve PolesCount=4 KnotsCount=2 Degree=3 IsPeriodic=0
    g2: BSplineCurve PolesCount=4 KnotsCount=2 Degree=3 IsPeriodic=0
  constraints (2):
    c: Coincident(g0,g1)
    c: Coincident(g1,g2)
FEATURE [Sketcher::SketchObject] Sketch046
  sketch-geometry (2):
    g0: BSplineCurve PolesCount=4 KnotsCount=2 Degree=3 IsPeriodic=0
    g1: BSplineCurve PolesCount=4 KnotsCount=2 Degree=3 IsPeriodic=0
  constraints (1):
    c: Coincident(g0,g1)
FEATURE [Sketcher::SketchObject] Sketch047
  sketch-geometry (1):
    g0: BSplineCurve PolesCount=4 KnotsCount=2 Degree=3 IsPeriodic=0
FEATURE [Sketcher::SketchObject] Sketch048
  sketch-geometry (1):
    g0: BSplineCurve PolesCount=4 KnotsCount=2 Degree=3 IsPeriodic=0
FEATURE [Sketcher::SketchObject] Sketch049
  sketch-geometry (2):
    g0: BSplineCurve PolesCount=4 KnotsCount=2 Degree=3 IsPeriodic=0
    g1: BSplineCurve PolesCount=4 KnotsCount=2 Degree=3 IsPeriodic=0
  constraints (1):
    c: Coincident(g0,g1)
FEATURE [Sketcher::SketchObject] Sketch050
  sketch-geometry (3):
    g0: BSplineCurve PolesCount=4 KnotsCount=2 Degree=3 IsPeriodic=0
    g1: BSplineCurve PolesCount=4 KnotsCount=2 Degree=3 IsPeriodic=0
    g2: BSplineCurve PolesCount=4 KnotsCount=2 Degree=3 IsPeriodic=0
  constraints (2):
    c: Coincident(g0,g1)
    c: Coincident(g1,g2)
FEATURE [Sketcher::SketchObject] Sketch051
  sketch-geometry (1):
    g0: BSplineCurve PolesCount=4 KnotsCount=2 Degree=3 IsPeriodic=0
FEATURE [Sketcher::SketchObject] Sketch052
  sketch-geometry (1):
    g0: BSplineCurve PolesCount=4 KnotsCount=2 Degree=3 IsPeriodic=0
FEATURE [Sketcher::SketchObject] Sketch053
  sketch-geometry (3):
    g0: BSplineCurve PolesCount=4 KnotsCount=2 Degree=3 IsPeriodic=0
    g1: BSplineCurve PolesCount=4 KnotsCount=2 Degree=3 IsPeriodic=0
    g2: BSplineCurve PolesCount=4 KnotsCount=2 Degree=3 IsPeriodic=0
  constraints (2):
    c: Coincident(g0,g1)
    c: Coincident(g1,g2)
FEATURE [Sketcher::SketchObject] Sketch054
  sketch-geometry (1):
    g0: BSplineCurve PolesCount=4 KnotsCount=2 Degree=3 IsPeriodic=0
FEATURE [Sketcher::SketchObject] Sketch055
  sketch-geometry (3):
    g0: BSplineCurve PolesCount=4 KnotsCount=2 Degree=3 IsPeriodic=0
    g1: BSplineCurve PolesCount=4 KnotsCount=2 Degree=3 IsPeriodic=0
    g2: BSplineCurve PolesCount=4 KnotsCount=2 Degree=3 IsPeriodic=0
  constraints (2):
    c: Coincident(g0,g1)
    c: Coincident(g1,g2)
FEATURE [Sketcher::SketchObject] Sketch056
  sketch-geometry (3):
    g0: BSplineCurve PolesCount=4 KnotsCount=2 Degree=3 IsPeriodic=0
    g1: BSplineCurve PolesCount=4 KnotsCount=2 Degree=3 IsPeriodic=0
    g2: BSplineCurve PolesCount=4 KnotsCount=2 Degree=3 IsPeriodic=0
  constraints (2):
    c: Coincident(g0,g1)
    c: Coincident(g1,g2)
FEATURE [Sketcher::SketchObject] Sketch057
  sketch-geometry (1):
    g0: BSplineCurve PolesCount=4 KnotsCount=2 Degree=3 IsPeriodic=0
FEATURE [Sketcher::SketchObject] Sketch058
  sketch-geometry (3):
    g0: BSplineCurve PolesCount=4 KnotsCount=2 Degree=3 IsPeriodic=0
    g1: BSplineCurve PolesCount=4 KnotsCount=2 Degree=3 IsPeriodic=0
    g2: BSplineCurve PolesCount=4 KnotsCount=2 Degree=3 IsPeriodic=0
  constraints (2):
    c: Coincident(g0,g1)
    c: Coincident(g1,g2)
FEATURE [Sketcher::SketchObject] Sketch059
  sketch-geometry (1):
    g0: BSplineCurve PolesCount=4 KnotsCount=2 Degree=3 IsPeriodic=0
FEATURE [Sketcher::SketchObject] Sketch060
  sketch-geometry (2):
    g0: BSplineCurve PolesCount=4 KnotsCount=2 Degree=3 IsPeriodic=0
    g1: BSplineCurve PolesCount=4 KnotsCount=2 Degree=3 IsPeriodic=0
  constraints (1):
    c: Coincident(g0,g1)
FEATURE [Sketcher::SketchObject] Sketch061
  sketch-geometry (2):
    g0: BSplineCurve PolesCount=4 KnotsCount=2 Degree=3 IsPeriodic=0
    g1: BSplineCurve PolesCount=4 KnotsCount=2 Degree=3 IsPeriodic=0
  constraints (1):
    c: Coincident(g0,g1)
FEATURE [Sketcher::SketchObject] Sketch062
  sketch-geometry (1):
    g0: BSplineCurve PolesCount=4 KnotsCount=2 Degree=3 IsPeriodic=0
FEATURE [Sketcher::SketchObject] Sketch063
  sketch-geometry (1):
    g0: BSplineCurve PolesCount=4 KnotsCount=2 Degree=3 IsPeriodic=0
FEATURE [Sketcher::SketchObject] Sketch064
  sketch-geometry (3):
    g0: BSplineCurve PolesCount=4 KnotsCount=2 Degree=3 IsPeriodic=0
    g1: BSplineCurve PolesCount=4 KnotsCount=2 Degree=3 IsPeriodic=0
    g2: BSplineCurve PolesCount=4 KnotsCount=2 Degree=3 IsPeriodic=0
  constraints (2):
    c: Coincident(g0,g1)
    c: Coincident(g1,g2)
FEATURE [Sketcher::SketchObject] Sketch065
  sketch-geometry (3):
    g0: BSplineCurve PolesCount=4 KnotsCount=2 Degree=3 IsPeriodic=0
    g1: BSplineCurve PolesCount=4 KnotsCount=2 Degree=3 IsPeriodic=0
    g2: BSplineCurve PolesCount=4 KnotsCount=2 Degree=3 IsPeriodic=0
  constraints (2):
    c: Coincident(g0,g1)
    c: Coincident(g1,g2)
FEATURE [Sketcher::SketchObject] Sketch066
  sketch-geometry (1):
    g0: BSplineCurve PolesCount=4 KnotsCount=2 Degree=3 IsPeriodic=0
FEATURE [Sketcher::SketchObject] Sketch067
  sketch-geometry (3):
    g0: BSplineCurve PolesCount=4 KnotsCount=2 Degree=3 IsPeriodic=0
    g1: BSplineCurve PolesCount=4 KnotsCount=2 Degree=3 IsPeriodic=0
    g2: BSplineCurve PolesCount=4 KnotsCount=2 Degree=3 IsPeriodic=0
  constraints (2):
    c: Coincident(g0,g1)
    c: Coincident(g1,g2)
FEATURE [Sketcher::SketchObject] Sketch068
  sketch-geometry (3):
    g0: BSplineCurve PolesCount=4 KnotsCount=2 Degree=3 IsPeriodic=0
    g1: BSplineCurve PolesCount=4 KnotsCount=2 Degree=3 IsPeriodic=0
    g2: BSplineCurve PolesCount=4 KnotsCount=2 Degree=3 IsPeriodic=0
  constraints (2):
    c: Coincident(g0,g1)
    c: Coincident(g1,g2)
FEATURE [Sketcher::SketchObject] Sketch069
  sketch-geometry (3):
    g0: BSplineCurve PolesCount=4 KnotsCount=2 Degree=3 IsPeriodic=0
    g1: BSplineCurve PolesCount=4 KnotsCount=2 Degree=3 IsPeriodic=0
    g2: BSplineCurve PolesCount=4 KnotsCount=2 Degree=3 IsPeriodic=0
  constraints (2):
    c: Coincident(g0,g1)
    c: Coincident(g1,g2)
FEATURE [Sketcher::SketchObject] Sketch070
  sketch-geometry (2):
    g0: BSplineCurve PolesCount=4 KnotsCount=2 Degree=3 IsPeriodic=0
    g1: BSplineCurve PolesCount=4 KnotsCount=2 Degree=3 IsPeriodic=0
  constraints (1):
    c: Coincident(g0,g1)
FEATURE [Sketcher::SketchObject] Sketch071
  sketch-geometry (1):
    g0: BSplineCurve PolesCount=4 KnotsCount=2 Degree=3 IsPeriodic=0
FEATURE [Sketcher::SketchObject] Sketch072
  sketch-geometry (1):
    g0: BSplineCurve PolesCount=4 KnotsCount=2 Degree=3 IsPeriodic=0
FEATURE [Sketcher::SketchObject] Sketch073
  sketch-geometry (3):
    g0: BSplineCurve PolesCount=4 KnotsCount=2 Degree=3 IsPeriodic=0
    g1: BSplineCurve PolesCount=4 KnotsCount=2 Degree=3 IsPeriodic=0
    g2: BSplineCurve PolesCount=4 KnotsCount=2 Degree=3 IsPeriodic=0
  constraints (2):
    c: Coincident(g0,g1)
    c: Coincident(g1,g2)
FEATURE [Sketcher::SketchObject] Sketch074
  sketch-geometry (3):
    g0: BSplineCurve PolesCount=4 KnotsCount=2 Degree=3 IsPeriodic=0
    g1: BSplineCurve PolesCount=4 KnotsCount=2 Degree=3 IsPeriodic=0
    g2: BSplineCurve PolesCount=4 KnotsCount=2 Degree=3 IsPeriodic=0
  constraints (2):
    c: Coincident(g0,g1)
    c: Coincident(g1,g2)
FEATURE [Sketcher::SketchObject] Sketch075
  sketch-geometry (1):
    g0: BSplineCurve PolesCount=4 KnotsCount=2 Degree=3 IsPeriodic=0
FEATURE [Sketcher::SketchObject] Sketch076
  sketch-geometry (1):
    g0: BSplineCurve PolesCount=4 KnotsCount=2 Degree=3 IsPeriodic=0
FEATURE [Sketcher::SketchObject] Sketch077
  sketch-geometry (1):
    g0: BSplineCurve PolesCount=4 KnotsCount=2 Degree=3 IsPeriodic=0
FEATURE [Sketcher::SketchObject] Sketch078
  sketch-geometry (1):
    g0: BSplineCurve PolesCount=4 KnotsCount=2 Degree=3 IsPeriodic=0
FEATURE [Sketcher::SketchObject] Sketch079
  sketch-geometry (2):
    g0: BSplineCurve PolesCount=4 KnotsCount=2 Degree=3 IsPeriodic=0
    g1: BSplineCurve PolesCount=4 KnotsCount=2 Degree=3 IsPeriodic=0
  constraints (1):
    c: Coincident(g0,g1)
FEATURE [Sketcher::SketchObject] Sketch080
  sketch-geometry (3):
    g0: BSplineCurve PolesCount=4 KnotsCount=2 Degree=3 IsPeriodic=0
    g1: BSplineCurve PolesCount=4 KnotsCount=2 Degree=3 IsPeriodic=0
    g2: BSplineCurve PolesCount=4 KnotsCount=2 Degree=3 IsPeriodic=0
  constraints (2):
    c: Coincident(g0,g1)
    c: Coincident(g1,g2)
FEATURE [Sketcher::SketchObject] Sketch081
  sketch-geometry (1):
    g0: BSplineCurve PolesCount=4 KnotsCount=2 Degree=3 IsPeriodic=0
FEATURE [Sketcher::SketchObject] Sketch082
  sketch-geometry (2):
    g0: BSplineCurve PolesCount=4 KnotsCount=2 Degree=3 IsPeriodic=0
    g1: BSplineCurve PolesCount=4 KnotsCount=2 Degree=3 IsPeriodic=0
  constraints (1):
    c: Coincident(g0,g1)
FEATURE [Sketcher::SketchObject] Sketch083
  sketch-geometry (3):
    g0: BSplineCurve PolesCount=4 KnotsCount=2 Degree=3 IsPeriodic=0
    g1: BSplineCurve PolesCount=4 KnotsCount=2 Degree=3 IsPeriodic=0
    g2: BSplineCurve PolesCount=4 KnotsCount=2 Degree=3 IsPeriodic=0
  constraints (2):
    c: Coincident(g0,g1)
    c: Coincident(g1,g2)
FEATURE [Sketcher::SketchObject] Sketch084
  sketch-geometry (3):
    g0: BSplineCurve PolesCount=4 KnotsCount=2 Degree=3 IsPeriodic=0
    g1: BSplineCurve PolesCount=4 KnotsCount=2 Degree=3 IsPeriodic=0
    g2: BSplineCurve PolesCount=4 KnotsCount=2 Degree=3 IsPeriodic=0
  constraints (2):
    c: Coincident(g0,g1)
    c: Coincident(g1,g2)
FEATURE [Sketcher::SketchObject] Sketch085
  sketch-geometry (3):
    g0: BSplineCurve PolesCount=4 KnotsCount=2 Degree=3 IsPeriodic=0
    g1: BSplineCurve PolesCount=4 KnotsCount=2 Degree=3 IsPeriodic=0
    g2: BSplineCurve PolesCount=4 KnotsCount=2 Degree=3 IsPeriodic=0
  constraints (2):
    c: Coincident(g0,g1)
    c: Coincident(g1,g2)
FEATURE [Sketcher::SketchObject] Sketch086
  sketch-geometry (1):
    g0: BSplineCurve PolesCount=4 KnotsCount=2 Degree=3 IsPeriodic=0
FEATURE [Sketcher::SketchObject] Sketch087
  sketch-geometry (3):
    g0: BSplineCurve PolesCount=4 KnotsCount=2 Degree=3 IsPeriodic=0
    g1: BSplineCurve PolesCount=4 KnotsCount=2 Degree=3 IsPeriodic=0
    g2: BSplineCurve PolesCount=4 KnotsCount=2 Degree=3 IsPeriodic=0
  constraints (2):
    c: Coincident(g0,g1)
    c: Coincident(g1,g2)
FEATURE [Sketcher::SketchObject] Sketch088
  sketch-geometry (2):
    g0: BSplineCurve PolesCount=4 KnotsCount=2 Degree=3 IsPeriodic=0
    g1: BSplineCurve PolesCount=4 KnotsCount=2 Degree=3 IsPeriodic=0
  constraints (1):
    c: Coincident(g0,g1)
FEATURE [Sketcher::SketchObject] Sketch089
  sketch-geometry (1):
    g0: BSplineCurve PolesCount=4 KnotsCount=2 Degree=3 IsPeriodic=0
FEATURE [Sketcher::SketchObject] Sketch090
  sketch-geometry (1):
    g0: BSplineCurve PolesCount=4 KnotsCount=2 Degree=3 IsPeriodic=0
FEATURE [Sketcher::SketchObject] Sketch091
  sketch-geometry (2):
    g0: BSplineCurve PolesCount=4 KnotsCount=2 Degree=3 IsPeriodic=0
    g1: BSplineCurve PolesCount=4 KnotsCount=2 Degree=3 IsPeriodic=0
  constraints (1):
    c: Coincident(g0,g1)
FEATURE [Sketcher::SketchObject] Sketch092
  sketch-geometry (1):
    g0: BSplineCurve PolesCount=4 KnotsCount=2 Degree=3 IsPeriodic=0
FEATURE [Sketcher::SketchObject] Sketch093
  sketch-geometry (1):
    g0: BSplineCurve PolesCount=4 KnotsCount=2 Degree=3 IsPeriodic=0
FEATURE [Sketcher::SketchObject] Sketch094
  sketch-geometry (3):
    g0: BSplineCurve PolesCount=4 KnotsCount=2 Degree=3 IsPeriodic=0
    g1: BSplineCurve PolesCount=4 KnotsCount=2 Degree=3 IsPeriodic=0
    g2: BSplineCurve PolesCount=4 KnotsCount=2 Degree=3 IsPeriodic=0
  constraints (2):
    c: Coincident(g0,g1)
    c: Coincident(g1,g2)
FEATURE [Sketcher::SketchObject] Sketch095
  sketch-geometry (1):
    g0: BSplineCurve PolesCount=4 KnotsCount=2 Degree=3 IsPeriodic=0
FEATURE [Sketcher::SketchObject] Sketch096
  sketch-geometry (3):
    g0: BSplineCurve PolesCount=4 KnotsCount=2 Degree=3 IsPeriodic=0
    g1: BSplineCurve PolesCount=4 KnotsCount=2 Degree=3 IsPeriodic=0
    g2: BSplineCurve PolesCount=4 KnotsCount=2 Degree=3 IsPeriodic=0
  constraints (2):
    c: Coincident(g0,g1)
    c: Coincident(g1,g2)
FEATURE [Sketcher::SketchObject] Sketch097
  sketch-geometry (2):
    g0: BSplineCurve PolesCount=4 KnotsCount=2 Degree=3 IsPeriodic=0
    g1: BSplineCurve PolesCount=4 KnotsCount=2 Degree=3 IsPeriodic=0
  constraints (1):
    c: Coincident(g0,g1)
FEATURE [Sketcher::SketchObject] Sketch098
  sketch-geometry (1):
    g0: BSplineCurve PolesCount=4 KnotsCount=2 Degree=3 IsPeriodic=0
FEATURE [Sketcher::SketchObject] Sketch099
  sketch-geometry (1):
    g0: BSplineCurve PolesCount=4 KnotsCount=2 Degree=3 IsPeriodic=0
FEATURE [Sketcher::SketchObject] Sketch100
  sketch-geometry (3):
    g0: BSplineCurve PolesCount=4 KnotsCount=2 Degree=3 IsPeriodic=0
    g1: BSplineCurve PolesCount=4 KnotsCount=2 Degree=3 IsPeriodic=0
    g2: BSplineCurve PolesCount=4 KnotsCount=2 Degree=3 IsPeriodic=0
  constraints (2):
    c: Coincident(g0,g1)
    c: Coincident(g1,g2)
FEATURE [Sketcher::SketchObject] Sketch101
  sketch-geometry (3):
    g0: BSplineCurve PolesCount=4 KnotsCount=2 Degree=3 IsPeriodic=0
    g1: BSplineCurve PolesCount=4 KnotsCount=2 Degree=3 IsPeriodic=0
    g2: BSplineCurve PolesCount=4 KnotsCount=2 Degree=3 IsPeriodic=0
  constraints (2):
    c: Coincident(g0,g1)
    c: Coincident(g1,g2)
FEATURE [Sketcher::SketchObject] Sketch102
  sketch-geometry (1):
    g0: BSplineCurve PolesCount=4 KnotsCount=2 Degree=3 IsPeriodic=0
FEATURE [Sketcher::SketchObject] Sketch103
  sketch-geometry (3):
    g0: BSplineCurve PolesCount=4 KnotsCount=2 Degree=3 IsPeriodic=0
    g1: BSplineCurve PolesCount=4 KnotsCount=2 Degree=3 IsPeriodic=0
    g2: BSplineCurve PolesCount=4 KnotsCount=2 Degree=3 IsPeriodic=0
  constraints (2):
    c: Coincident(g0,g1)
    c: Coincident(g1,g2)
FEATURE [Sketcher::SketchObject] Sketch104
  sketch-geometry (1):
    g0: BSplineCurve PolesCount=4 KnotsCount=2 Degree=3 IsPeriodic=0
FEATURE [Sketcher::SketchObject] Sketch105
  sketch-geometry (1):
    g0: BSplineCurve PolesCount=4 KnotsCount=2 Degree=3 IsPeriodic=0
FEATURE [Sketcher::SketchObject] Sketch106
  sketch-geometry (2):
    g0: BSplineCurve PolesCount=4 KnotsCount=2 Degree=3 IsPeriodic=0
    g1: BSplineCurve PolesCount=4 KnotsCount=2 Degree=3 IsPeriodic=0
  constraints (1):
    c: Coincident(g0,g1)
FEATURE [Sketcher::SketchObject] Sketch107
  sketch-geometry (3):
    g0: BSplineCurve PolesCount=4 KnotsCount=2 Degree=3 IsPeriodic=0
    g1: BSplineCurve PolesCount=4 KnotsCount=2 Degree=3 IsPeriodic=0
    g2: BSplineCurve PolesCount=4 KnotsCount=2 Degree=3 IsPeriodic=0
  constraints (2):
    c: Coincident(g0,g1)
    c: Coincident(g1,g2)
FEATURE [Sketcher::SketchObject] Sketch108
  sketch-geometry (2):
    g0: BSplineCurve PolesCount=4 KnotsCount=2 Degree=3 IsPeriodic=0
    g1: BSplineCurve PolesCount=4 KnotsCount=2 Degree=3 IsPeriodic=0
  constraints (1):
    c: Coincident(g0,g1)
FEATURE [Sketcher::SketchObject] Sketch109
  sketch-geometry (3):
    g0: BSplineCurve PolesCount=4 KnotsCount=2 Degree=3 IsPeriodic=0
    g1: BSplineCurve PolesCount=4 KnotsCount=2 Degree=3 IsPeriodic=0
    g2: BSplineCurve PolesCount=4 KnotsCount=2 Degree=3 IsPeriodic=0
  constraints (2):
    c: Coincident(g0,g1)
    c: Coincident(g1,g2)
FEATURE [Sketcher::SketchObject] Sketch110
  sketch-geometry (3):
    g0: BSplineCurve PolesCount=4 KnotsCount=2 Degree=3 IsPeriodic=0
    g1: BSplineCurve PolesCount=4 KnotsCount=2 Degree=3 IsPeriodic=0
    g2: BSplineCurve PolesCount=4 KnotsCount=2 Degree=3 IsPeriodic=0
  constraints (2):
    c: Coincident(g0,g1)
    c: Coincident(g1,g2)
FEATURE [Sketcher::SketchObject] Sketch111
  sketch-geometry (1):
    g0: BSplineCurve PolesCount=4 KnotsCount=2 Degree=3 IsPeriodic=0
FEATURE [Sketcher::SketchObject] Sketch112
  sketch-geometry (4):
    g0: BSplineCurve PolesCount=4 KnotsCount=2 Degree=3 IsPeriodic=0
    g1: BSplineCurve PolesCount=4 KnotsCount=2 Degree=3 IsPeriodic=0
    g2: BSplineCurve PolesCount=4 KnotsCount=2 Degree=3 IsPeriodic=0
    g3: BSplineCurve PolesCount=4 KnotsCount=2 Degree=3 IsPeriodic=0
  constraints (3):
    c: Coincident(g0,g1)
    c: Coincident(g1,g2)
    c: Coincident(g2,g3)
FEATURE [Sketcher::SketchObject] Sketch113
  sketch-geometry (1):
    g0: BSplineCurve PolesCount=4 KnotsCount=2 Degree=3 IsPeriodic=0
FEATURE [Sketcher::SketchObject] Sketch114
  sketch-geometry (3):
    g0: BSplineCurve PolesCount=4 KnotsCount=2 Degree=3 IsPeriodic=0
    g1: BSplineCurve PolesCount=4 KnotsCount=2 Degree=3 IsPeriodic=0
    g2: BSplineCurve PolesCount=4 KnotsCount=2 Degree=3 IsPeriodic=0
  constraints (2):
    c: Coincident(g0,g1)
    c: Coincident(g1,g2)
FEATURE [Sketcher::SketchObject] Sketch115
  sketch-geometry (3):
    g0: BSplineCurve PolesCount=4 KnotsCount=2 Degree=3 IsPeriodic=0
    g1: BSplineCurve PolesCount=4 KnotsCount=2 Degree=3 IsPeriodic=0
    g2: BSplineCurve PolesCount=4 KnotsCount=2 Degree=3 IsPeriodic=0
  constraints (2):
    c: Coincident(g0,g1)
    c: Coincident(g1,g2)
FEATURE [Sketcher::SketchObject] Sketch116
  sketch-geometry (1):
    g0: BSplineCurve PolesCount=4 KnotsCount=2 Degree=3 IsPeriodic=0
FEATURE [Sketcher::SketchObject] Sketch117
  sketch-geometry (1):
    g0: BSplineCurve PolesCount=4 KnotsCount=2 Degree=3 IsPeriodic=0
FEATURE [Sketcher::SketchObject] Sketch118
  sketch-geometry (3):
    g0: BSplineCurve PolesCount=4 KnotsCount=2 Degree=3 IsPeriodic=0
    g1: BSplineCurve PolesCount=4 KnotsCount=2 Degree=3 IsPeriodic=0
    g2: BSplineCurve PolesCount=4 KnotsCount=2 Degree=3 IsPeriodic=0
  constraints (2):
    c: Coincident(g0,g1)
    c: Coincident(g1,g2)
FEATURE [Sketcher::SketchObject] Sketch119
  sketch-geometry (3):
    g0: BSplineCurve PolesCount=4 KnotsCount=2 Degree=3 IsPeriodic=0
    g1: BSplineCurve PolesCount=4 KnotsCount=2 Degree=3 IsPeriodic=0
    g2: BSplineCurve PolesCount=4 KnotsCount=2 Degree=3 IsPeriodic=0
  constraints (2):
    c: Coincident(g0,g1)
    c: Coincident(g1,g2)
FEATURE [Sketcher::SketchObject] Sketch120
  sketch-geometry (1):
    g0: BSplineCurve PolesCount=4 KnotsCount=2 Degree=3 IsPeriodic=0
FEATURE [Sketcher::SketchObject] Sketch121
  sketch-geometry (4):
    g0: BSplineCurve PolesCount=4 KnotsCount=2 Degree=3 IsPeriodic=0
    g1: BSplineCurve PolesCount=4 KnotsCount=2 Degree=3 IsPeriodic=0
    g2: BSplineCurve PolesCount=4 KnotsCount=2 Degree=3 IsPeriodic=0
    g3: BSplineCurve PolesCount=4 KnotsCount=2 Degree=3 IsPeriodic=0
  constraints (3):
    c: Coincident(g0,g1)
    c: Coincident(g1,g2)
    c: Coincident(g2,g3)
FEATURE [Sketcher::SketchObject] Sketch122
  sketch-geometry (1):
    g0: BSplineCurve PolesCount=4 KnotsCount=2 Degree=3 IsPeriodic=0
FEATURE [Sketcher::SketchObject] Sketch123
  sketch-geometry (3):
    g0: BSplineCurve PolesCount=4 KnotsCount=2 Degree=3 IsPeriodic=0
    g1: BSplineCurve PolesCount=4 KnotsCount=2 Degree=3 IsPeriodic=0
    g2: BSplineCurve PolesCount=4 KnotsCount=2 Degree=3 IsPeriodic=0
  constraints (2):
    c: Coincident(g0,g1)
    c: Coincident(g1,g2)
FEATURE [Sketcher::SketchObject] Sketch124
  sketch-geometry (1):
    g0: BSplineCurve PolesCount=4 KnotsCount=2 Degree=3 IsPeriodic=0
FEATURE [Sketcher::SketchObject] Sketch125
  sketch-geometry (1):
    g0: BSplineCurve PolesCount=4 KnotsCount=2 Degree=3 IsPeriodic=0
FEATURE [Sketcher::SketchObject] Sketch126
  sketch-geometry (1):
    g0: BSplineCurve PolesCount=4 KnotsCount=2 Degree=3 IsPeriodic=0
FEATURE [Sketcher::SketchObject] Sketch127
  sketch-geometry (2):
    g0: BSplineCurve PolesCount=4 KnotsCount=2 Degree=3 IsPeriodic=0
    g1: BSplineCurve PolesCount=4 KnotsCount=2 Degree=3 IsPeriodic=0
  constraints (1):
    c: Coincident(g0,g1)
FEATURE [Sketcher::SketchObject] Sketch128
  sketch-geometry (3):
    g0: BSplineCurve PolesCount=4 KnotsCount=2 Degree=3 IsPeriodic=0
    g1: BSplineCurve PolesCount=4 KnotsCount=2 Degree=3 IsPeriodic=0
    g2: BSplineCurve PolesCount=4 KnotsCount=2 Degree=3 IsPeriodic=0
  constraints (2):
    c: Coincident(g0,g1)
    c: Coincident(g1,g2)
FEATURE [Sketcher::SketchObject] Sketch129
  sketch-geometry (1):
    g0: BSplineCurve PolesCount=4 KnotsCount=2 Degree=3 IsPeriodic=0
FEATURE [Sketcher::SketchObject] Sketch130
  sketch-geometry (4):
    g0: BSplineCurve PolesCount=4 KnotsCount=2 Degree=3 IsPeriodic=0
    g1: BSplineCurve PolesCount=4 KnotsCount=2 Degree=3 IsPeriodic=0
    g2: BSplineCurve PolesCount=4 KnotsCount=2 Degree=3 IsPeriodic=0
    g3: BSplineCurve PolesCount=4 KnotsCount=2 Degree=3 IsPeriodic=0
  constraints (3):
    c: Coincident(g0,g1)
    c: Coincident(g1,g2)
    c: Coincident(g2,g3)
FEATURE [Sketcher::SketchObject] Sketch131
  sketch-geometry (1):
    g0: BSplineCurve PolesCount=4 KnotsCount=2 Degree=3 IsPeriodic=0
FEATURE [Sketcher::SketchObject] Sketch132
  sketch-geometry (3):
    g0: BSplineCurve PolesCount=4 KnotsCount=2 Degree=3 IsPeriodic=0
    g1: BSplineCurve PolesCount=4 KnotsCount=2 Degree=3 IsPeriodic=0
    g2: BSplineCurve PolesCount=4 KnotsCount=2 Degree=3 IsPeriodic=0
  constraints (2):
    c: Coincident(g0,g1)
    c: Coincident(g1,g2)
FEATURE [Sketcher::SketchObject] Sketch133
  sketch-geometry (2):
    g0: BSplineCurve PolesCount=4 KnotsCount=2 Degree=3 IsPeriodic=0
    g1: BSplineCurve PolesCount=4 KnotsCount=2 Degree=3 IsPeriodic=0
  constraints (1):
    c: Coincident(g0,g1)
FEATURE [Sketcher::SketchObject] Sketch134
  sketch-geometry (3):
    g0: BSplineCurve PolesCount=4 KnotsCount=2 Degree=3 IsPeriodic=0
    g1: BSplineCurve PolesCount=4 KnotsCount=2 Degree=3 IsPeriodic=0
    g2: BSplineCurve PolesCount=4 KnotsCount=2 Degree=3 IsPeriodic=0
  constraints (2):
    c: Coincident(g0,g1)
    c: Coincident(g1,g2)
FEATURE [Sketcher::SketchObject] Sketch135
  sketch-geometry (1):
    g0: BSplineCurve PolesCount=4 KnotsCount=2 Degree=3 IsPeriodic=0
FEATURE [Sketcher::SketchObject] Sketch136
  sketch-geometry (2):
    g0: BSplineCurve PolesCount=4 KnotsCount=2 Degree=3 IsPeriodic=0
    g1: BSplineCurve PolesCount=4 KnotsCount=2 Degree=3 IsPeriodic=0
  constraints (1):
    c: Coincident(g0,g1)
FEATURE [Sketcher::SketchObject] Sketch137
  sketch-geometry (3):
    g0: BSplineCurve PolesCount=4 KnotsCount=2 Degree=3 IsPeriodic=0
    g1: BSplineCurve PolesCount=4 KnotsCount=2 Degree=3 IsPeriodic=0
    g2: BSplineCurve PolesCount=4 KnotsCount=2 Degree=3 IsPeriodic=0
  constraints (2):
    c: Coincident(g0,g1)
    c: Coincident(g1,g2)
FEATURE [Sketcher::SketchObject] Sketch138
  sketch-geometry (1):
    g0: BSplineCurve PolesCount=4 KnotsCount=2 Degree=3 IsPeriodic=0
FEATURE [Sketcher::SketchObject] Sketch139
  sketch-geometry (3):
    g0: BSplineCurve PolesCount=4 KnotsCount=2 Degree=3 IsPeriodic=0
    g1: BSplineCurve PolesCount=4 KnotsCount=2 Degree=3 IsPeriodic=0
    g2: BSplineCurve PolesCount=4 KnotsCount=2 Degree=3 IsPeriodic=0
  constraints (2):
    c: Coincident(g0,g1)
    c: Coincident(g1,g2)
FEATURE [Sketcher::SketchObject] Sketch140
  sketch-geometry (1):
    g0: BSplineCurve PolesCount=4 KnotsCount=2 Degree=3 IsPeriodic=0
FEATURE [Sketcher::SketchObject] Sketch141
  sketch-geometry (3):
    g0: BSplineCurve PolesCount=4 KnotsCount=2 Degree=3 IsPeriodic=0
    g1: BSplineCurve PolesCount=4 KnotsCount=2 Degree=3 IsPeriodic=0
    g2: BSplineCurve PolesCount=4 KnotsCount=2 Degree=3 IsPeriodic=0
  constraints (2):
    c: Coincident(g0,g1)
    c: Coincident(g1,g2)
FEATURE [Sketcher::SketchObject] Sketch142
  sketch-geometry (2):
    g0: BSplineCurve PolesCount=4 KnotsCount=2 Degree=3 IsPeriodic=0
    g1: BSplineCurve PolesCount=4 KnotsCount=2 Degree=3 IsPeriodic=0
  constraints (1):
    c: Coincident(g0,g1)
FEATURE [Sketcher::SketchObject] Sketch143
  sketch-geometry (1):
    g0: BSplineCurve PolesCount=4 KnotsCount=2 Degree=3 IsPeriodic=0
FEATURE [Sketcher::SketchObject] Sketch144
  sketch-geometry (1):
    g0: BSplineCurve PolesCount=4 KnotsCount=2 Degree=3 IsPeriodic=0
FEATURE [Sketcher::SketchObject] Sketch145
  sketch-geometry (1):
    g0: BSplineCurve PolesCount=4 KnotsCount=2 Degree=3 IsPeriodic=0
FEATURE [Sketcher::SketchObject] Sketch146
  sketch-geometry (3):
    g0: BSplineCurve PolesCount=4 KnotsCount=2 Degree=3 IsPeriodic=0
    g1: BSplineCurve PolesCount=4 KnotsCount=2 Degree=3 IsPeriodic=0
    g2: BSplineCurve PolesCount=4 KnotsCount=2 Degree=3 IsPeriodic=0
  constraints (2):
    c: Coincident(g0,g1)
    c: Coincident(g1,g2)
FEATURE [Sketcher::SketchObject] Sketch147
  sketch-geometry (1):
    g0: BSplineCurve PolesCount=4 KnotsCount=2 Degree=3 IsPeriodic=0
FEATURE [Sketcher::SketchObject] Sketch148
  sketch-geometry (3):
    g0: BSplineCurve PolesCount=4 KnotsCount=2 Degree=3 IsPeriodic=0
    g1: BSplineCurve PolesCount=4 KnotsCount=2 Degree=3 IsPeriodic=0
    g2: BSplineCurve PolesCount=4 KnotsCount=2 Degree=3 IsPeriodic=0
  constraints (2):
    c: Coincident(g0,g1)
    c: Coincident(g1,g2)
FEATURE [Sketcher::SketchObject] Sketch149
  sketch-geometry (1):
    g0: BSplineCurve PolesCount=4 KnotsCount=2 Degree=3 IsPeriodic=0
FEATURE [Sketcher::SketchObject] Sketch150
  sketch-geometry (3):
    g0: BSplineCurve PolesCount=4 KnotsCount=2 Degree=3 IsPeriodic=0
    g1: BSplineCurve PolesCount=4 KnotsCount=2 Degree=3 IsPeriodic=0
    g2: BSplineCurve PolesCount=4 KnotsCount=2 Degree=3 IsPeriodic=0
  constraints (2):
    c: Coincident(g0,g1)
    c: Coincident(g1,g2)
FEATURE [Sketcher::SketchObject] Sketch151
  sketch-geometry (2):
    g0: BSplineCurve PolesCount=4 KnotsCount=2 Degree=3 IsPeriodic=0
    g1: BSplineCurve PolesCount=4 KnotsCount=2 Degree=3 IsPeriodic=0
  constraints (1):
    c: Coincident(g0,g1)
FEATURE [Sketcher::SketchObject] Sketch152
  sketch-geometry (1):
    g0: BSplineCurve PolesCount=4 KnotsCount=2 Degree=3 IsPeriodic=0
FEATURE [Sketcher::SketchObject] Sketch153
  sketch-geometry (2):
    g0: BSplineCurve PolesCount=4 KnotsCount=2 Degree=3 IsPeriodic=0
    g1: BSplineCurve PolesCount=4 KnotsCount=2 Degree=3 IsPeriodic=0
  constraints (1):
    c: Coincident(g0,g1)
FEATURE [Sketcher::SketchObject] Sketch154
  sketch-geometry (2):
    g0: BSplineCurve PolesCount=4 KnotsCount=2 Degree=3 IsPeriodic=0
    g1: BSplineCurve PolesCount=4 KnotsCount=2 Degree=3 IsPeriodic=0
  constraints (1):
    c: Coincident(g0,g1)
FEATURE [Sketcher::SketchObject] Sketch155
  sketch-geometry (3):
    g0: BSplineCurve PolesCount=4 KnotsCount=2 Degree=3 IsPeriodic=0
    g1: BSplineCurve PolesCount=4 KnotsCount=2 Degree=3 IsPeriodic=0
    g2: BSplineCurve PolesCount=4 KnotsCount=2 Degree=3 IsPeriodic=0
  constraints (2):
    c: Coincident(g0,g1)
    c: Coincident(g1,g2)
FEATURE [Sketcher::SketchObject] Sketch156
  sketch-geometry (1):
    g0: BSplineCurve PolesCount=4 KnotsCount=2 Degree=3 IsPeriodic=0
FEATURE [Sketcher::SketchObject] Sketch157
  sketch-geometry (3):
    g0: BSplineCurve PolesCount=4 KnotsCount=2 Degree=3 IsPeriodic=0
    g1: BSplineCurve PolesCount=4 KnotsCount=2 Degree=3 IsPeriodic=0
    g2: BSplineCurve PolesCount=4 KnotsCount=2 Degree=3 IsPeriodic=0
  constraints (2):
    c: Coincident(g0,g1)
    c: Coincident(g1,g2)
FEATURE [Sketcher::SketchObject] Sketch158
  sketch-geometry (1):
    g0: BSplineCurve PolesCount=4 KnotsCount=2 Degree=3 IsPeriodic=0
FEATURE [Sketcher::SketchObject] Sketch159
  sketch-geometry (1):
    g0: BSplineCurve PolesCount=4 KnotsCount=2 Degree=3 IsPeriodic=0
FEATURE [Sketcher::SketchObject] Sketch160
  sketch-geometry (2):
    g0: BSplineCurve PolesCount=4 KnotsCount=2 Degree=3 IsPeriodic=0
    g1: BSplineCurve PolesCount=4 KnotsCount=2 Degree=3 IsPeriodic=0
  constraints (1):
    c: Coincident(g0,g1)
FEATURE [Sketcher::SketchObject] Sketch161
  sketch-geometry (1):
    g0: BSplineCurve PolesCount=4 KnotsCount=2 Degree=3 IsPeriodic=0
FEATURE [Sketcher::SketchObject] Sketch162
  sketch-geometry (3):
    g0: BSplineCurve PolesCount=4 KnotsCount=2 Degree=3 IsPeriodic=0
    g1: BSplineCurve PolesCount=4 KnotsCount=2 Degree=3 IsPeriodic=0
    g2: BSplineCurve PolesCount=4 KnotsCount=2 Degree=3 IsPeriodic=0
  constraints (2):
    c: Coincident(g0,g1)
    c: Coincident(g1,g2)
FEATURE [Sketcher::SketchObject] Sketch163
  sketch-geometry (3):
    g0: BSplineCurve PolesCount=4 KnotsCount=2 Degree=3 IsPeriodic=0
    g1: BSplineCurve PolesCount=4 KnotsCount=2 Degree=3 IsPeriodic=0
    g2: BSplineCurve PolesCount=4 KnotsCount=2 Degree=3 IsPeriodic=0
  constraints (2):
    c: Coincident(g0,g1)
    c: Coincident(g1,g2)
FEATURE [Sketcher::SketchObject] Sketch164
  sketch-geometry (1):
    g0: BSplineCurve PolesCount=4 KnotsCount=2 Degree=3 IsPeriodic=0
FEATURE [Sketcher::SketchObject] Sketch165
  sketch-geometry (1):
    g0: BSplineCurve PolesCount=4 KnotsCount=2 Degree=3 IsPeriodic=0
FEATURE [Sketcher::SketchObject] Sketch166
  sketch-geometry (2):
    g0: BSplineCurve PolesCount=4 KnotsCount=2 Degree=3 IsPeriodic=0
    g1: BSplineCurve PolesCount=4 KnotsCount=2 Degree=3 IsPeriodic=0
  constraints (1):
    c: Coincident(g0,g1)
FEATURE [Sketcher::SketchObject] Sketch167
  sketch-geometry (3):
    g0: BSplineCurve PolesCount=4 KnotsCount=2 Degree=3 IsPeriodic=0
    g1: BSplineCurve PolesCount=4 KnotsCount=2 Degree=3 IsPeriodic=0
    g2: BSplineCurve PolesCount=4 KnotsCount=2 Degree=3 IsPeriodic=0
  constraints (2):
    c: Coincident(g0,g1)
    c: Coincident(g1,g2)
FEATURE [Sketcher::SketchObject] Sketch168
  sketch-geometry (1):
    g0: BSplineCurve PolesCount=4 KnotsCount=2 Degree=3 IsPeriodic=0
FEATURE [Sketcher::SketchObject] Sketch169
  sketch-geometry (3):
    g0: BSplineCurve PolesCount=4 KnotsCount=2 Degree=3 IsPeriodic=0
    g1: BSplineCurve PolesCount=4 KnotsCount=2 Degree=3 IsPeriodic=0
    g2: BSplineCurve PolesCount=4 KnotsCount=2 Degree=3 IsPeriodic=0
  constraints (2):
    c: Coincident(g0,g1)
    c: Coincident(g1,g2)
FEATURE [Sketcher::SketchObject] Sketch170
  sketch-geometry (1):
    g0: BSplineCurve PolesCount=4 KnotsCount=2 Degree=3 IsPeriodic=0
FEATURE [Sketcher::SketchObject] Sketch171
  sketch-geometry (2):
    g0: BSplineCurve PolesCount=4 KnotsCount=2 Degree=3 IsPeriodic=0
    g1: BSplineCurve PolesCount=4 KnotsCount=2 Degree=3 IsPeriodic=0
  constraints (1):
    c: Coincident(g0,g1)
FEATURE [Sketcher::SketchObject] Sketch172
  sketch-geometry (3):
    g0: BSplineCurve PolesCount=4 KnotsCount=2 Degree=3 IsPeriodic=0
    g1: BSplineCurve PolesCount=4 KnotsCount=2 Degree=3 IsPeriodic=0
    g2: BSplineCurve PolesCount=4 KnotsCount=2 Degree=3 IsPeriodic=0
  constraints (2):
    c: Coincident(g0,g1)
    c: Coincident(g1,g2)
FEATURE [Sketcher::SketchObject] Sketch173
  sketch-geometry (1):
    g0: BSplineCurve PolesCount=4 KnotsCount=2 Degree=3 IsPeriodic=0
FEATURE [Sketcher::SketchObject] Sketch174
  sketch-geometry (3):
    g0: BSplineCurve PolesCount=4 KnotsCount=2 Degree=3 IsPeriodic=0
    g1: BSplineCurve PolesCount=4 KnotsCount=2 Degree=3 IsPeriodic=0
    g2: BSplineCurve PolesCount=4 KnotsCount=2 Degree=3 IsPeriodic=0
  constraints (2):
    c: Coincident(g0,g1)
    c: Coincident(g1,g2)
FEATURE [Sketcher::SketchObject] Sketch175
  sketch-geometry (1):
    g0: BSplineCurve PolesCount=4 KnotsCount=2 Degree=3 IsPeriodic=0
FEATURE [Sketcher::SketchObject] Sketch176
  sketch-geometry (1):
    g0: BSplineCurve PolesCount=4 KnotsCount=2 Degree=3 IsPeriodic=0
FEATURE [Sketcher::SketchObject] Sketch177
  sketch-geometry (3):
    g0: BSplineCurve PolesCount=4 KnotsCount=2 Degree=3 IsPeriodic=0
    g1: BSplineCurve PolesCount=4 KnotsCount=2 Degree=3 IsPeriodic=0
    g2: BSplineCurve PolesCount=4 KnotsCount=2 Degree=3 IsPeriodic=0
  constraints (2):
    c: Coincident(g0,g1)
    c: Coincident(g1,g2)
FEATURE [Sketcher::SketchObject] Sketch178
  sketch-geometry (3):
    g0: BSplineCurve PolesCount=4 KnotsCount=2 Degree=3 IsPeriodic=0
    g1: BSplineCurve PolesCount=4 KnotsCount=2 Degree=3 IsPeriodic=0
    g2: BSplineCurve PolesCount=4 KnotsCount=2 Degree=3 IsPeriodic=0
  constraints (2):
    c: Coincident(g0,g1)
    c: Coincident(g1,g2)
FEATURE [Sketcher::SketchObject] Sketch179
  sketch-geometry (1):
    g0: BSplineCurve PolesCount=4 KnotsCount=2 Degree=3 IsPeriodic=0
FEATURE [Sketcher::SketchObject] Sketch180
  sketch-geometry (1):
    g0: BSplineCurve PolesCount=4 KnotsCount=2 Degree=3 IsPeriodic=0
FEATURE [Sketcher::SketchObject] Sketch181
  sketch-geometry (2):
    g0: BSplineCurve PolesCount=4 KnotsCount=2 Degree=3 IsPeriodic=0
    g1: BSplineCurve PolesCount=4 KnotsCount=2 Degree=3 IsPeriodic=0
  constraints (1):
    c: Coincident(g0,g1)
FEATURE [Sketcher::SketchObject] Sketch182
  sketch-geometry (3):
    g0: BSplineCurve PolesCount=4 KnotsCount=2 Degree=3 IsPeriodic=0
    g1: BSplineCurve PolesCount=4 KnotsCount=2 Degree=3 IsPeriodic=0
    g2: BSplineCurve PolesCount=4 KnotsCount=2 Degree=3 IsPeriodic=0
  constraints (2):
    c: Coincident(g0,g1)
    c: Coincident(g1,g2)
FEATURE [Sketcher::SketchObject] Sketch183
  sketch-geometry (3):
    g0: BSplineCurve PolesCount=4 KnotsCount=2 Degree=3 IsPeriodic=0
    g1: BSplineCurve PolesCount=4 KnotsCount=2 Degree=3 IsPeriodic=0
    g2: BSplineCurve PolesCount=4 KnotsCount=2 Degree=3 IsPeriodic=0
  constraints (2):
    c: Coincident(g0,g1)
    c: Coincident(g1,g2)
FEATURE [Sketcher::SketchObject] Sketch184
  sketch-geometry (4):
    g0: BSplineCurve PolesCount=4 KnotsCount=2 Degree=3 IsPeriodic=0
    g1: BSplineCurve PolesCount=4 KnotsCount=2 Degree=3 IsPeriodic=0
    g2: BSplineCurve PolesCount=4 KnotsCount=2 Degree=3 IsPeriodic=0
    g3: BSplineCurve PolesCount=4 KnotsCount=2 Degree=3 IsPeriodic=0
  constraints (3):
    c: Coincident(g0,g1)
    c: Coincident(g1,g2)
    c: Coincident(g2,g3)
FEATURE [Sketcher::SketchObject] Sketch185
  sketch-geometry (1):
    g0: BSplineCurve PolesCount=4 KnotsCount=2 Degree=3 IsPeriodic=0
FEATURE [Sketcher::SketchObject] Sketch186
  sketch-geometry (1):
    g0: BSplineCurve PolesCount=4 KnotsCount=2 Degree=3 IsPeriodic=0
FEATURE [Sketcher::SketchObject] Sketch187
  sketch-geometry (3):
    g0: BSplineCurve PolesCount=4 KnotsCount=2 Degree=3 IsPeriodic=0
    g1: BSplineCurve PolesCount=4 KnotsCount=2 Degree=3 IsPeriodic=0
    g2: BSplineCurve PolesCount=4 KnotsCount=2 Degree=3 IsPeriodic=0
  constraints (2):
    c: Coincident(g0,g1)
    c: Coincident(g1,g2)
FEATURE [Sketcher::SketchObject] Sketch188
  sketch-geometry (3):
    g0: BSplineCurve PolesCount=4 KnotsCount=2 Degree=3 IsPeriodic=0
    g1: BSplineCurve PolesCount=4 KnotsCount=2 Degree=3 IsPeriodic=0
    g2: BSplineCurve PolesCount=4 KnotsCount=2 Degree=3 IsPeriodic=0
  constraints (2):
    c: Coincident(g0,g1)
    c: Coincident(g1,g2)
FEATURE [Sketcher::SketchObject] Sketch189
  sketch-geometry (1):
    g0: BSplineCurve PolesCount=4 KnotsCount=2 Degree=3 IsPeriodic=0
FEATURE [Sketcher::SketchObject] Sketch190
  sketch-geometry (2):
    g0: BSplineCurve PolesCount=4 KnotsCount=2 Degree=3 IsPeriodic=0
    g1: BSplineCurve PolesCount=4 KnotsCount=2 Degree=3 IsPeriodic=0
  constraints (1):
    c: Coincident(g0,g1)
FEATURE [Sketcher::SketchObject] Sketch191
  sketch-geometry (1):
    g0: BSplineCurve PolesCount=4 KnotsCount=2 Degree=3 IsPeriodic=0
FEATURE [Sketcher::SketchObject] Sketch192
  sketch-geometry (1):
    g0: BSplineCurve PolesCount=4 KnotsCount=2 Degree=3 IsPeriodic=0
FEATURE [Sketcher::SketchObject] Sketch193
  sketch-geometry (3):
    g0: BSplineCurve PolesCount=4 KnotsCount=2 Degree=3 IsPeriodic=0
    g1: BSplineCurve PolesCount=4 KnotsCount=2 Degree=3 IsPeriodic=0
    g2: BSplineCurve PolesCount=4 KnotsCount=2 Degree=3 IsPeriodic=0
  constraints (2):
    c: Coincident(g0,g1)
    c: Coincident(g1,g2)
FEATURE [Sketcher::SketchObject] Sketch194
  sketch-geometry (1):
    g0: BSplineCurve PolesCount=4 KnotsCount=2 Degree=3 IsPeriodic=0
FEATURE [Sketcher::SketchObject] Sketch195
  sketch-geometry (3):
    g0: BSplineCurve PolesCount=4 KnotsCount=2 Degree=3 IsPeriodic=0
    g1: BSplineCurve PolesCount=4 KnotsCount=2 Degree=3 IsPeriodic=0
    g2: BSplineCurve PolesCount=4 KnotsCount=2 Degree=3 IsPeriodic=0
  constraints (2):
    c: Coincident(g0,g1)
    c: Coincident(g1,g2)
FEATURE [Sketcher::SketchObject] Sketch196
  sketch-geometry (2):
    g0: BSplineCurve PolesCount=4 KnotsCount=2 Degree=3 IsPeriodic=0
    g1: BSplineCurve PolesCount=4 KnotsCount=2 Degree=3 IsPeriodic=0
  constraints (1):
    c: Coincident(g0,g1)
FEATURE [Sketcher::SketchObject] Sketch197
  sketch-geometry (1):
    g0: BSplineCurve PolesCount=4 KnotsCount=2 Degree=3 IsPeriodic=0
FEATURE [Sketcher::SketchObject] Sketch198
  sketch-geometry (1):
    g0: BSplineCurve PolesCount=4 KnotsCount=2 Degree=3 IsPeriodic=0
FEATURE [Sketcher::SketchObject] Sketch199
  sketch-geometry (3):
    g0: BSplineCurve PolesCount=4 KnotsCount=2 Degree=3 IsPeriodic=0
    g1: BSplineCurve PolesCount=4 KnotsCount=2 Degree=3 IsPeriodic=0
    g2: BSplineCurve PolesCount=4 KnotsCount=2 Degree=3 IsPeriodic=0
  constraints (2):
    c: Coincident(g0,g1)
    c: Coincident(g1,g2)
FEATURE [Sketcher::SketchObject] Sketch200
  sketch-geometry (3):
    g0: BSplineCurve PolesCount=4 KnotsCount=2 Degree=3 IsPeriodic=0
    g1: BSplineCurve PolesCount=4 KnotsCount=2 Degree=3 IsPeriodic=0
    g2: BSplineCurve PolesCount=4 KnotsCount=2 Degree=3 IsPeriodic=0
  constraints (2):
    c: Coincident(g0,g1)
    c: Coincident(g1,g2)
FEATURE [Sketcher::SketchObject] Sketch201
  sketch-geometry (1):
    g0: BSplineCurve PolesCount=4 KnotsCount=2 Degree=3 IsPeriodic=0
FEATURE [Sketcher::SketchObject] Sketch202
  sketch-geometry (3):
    g0: BSplineCurve PolesCount=4 KnotsCount=2 Degree=3 IsPeriodic=0
    g1: BSplineCurve PolesCount=4 KnotsCount=2 Degree=3 IsPeriodic=0
    g2: BSplineCurve PolesCount=4 KnotsCount=2 Degree=3 IsPeriodic=0
  constraints (2):
    c: Coincident(g0,g1)
    c: Coincident(g1,g2)
FEATURE [Sketcher::SketchObject] Sketch203
  sketch-geometry (1):
    g0: BSplineCurve PolesCount=4 KnotsCount=2 Degree=3 IsPeriodic=0
FEATURE [Sketcher::SketchObject] Sketch204
  sketch-geometry (3):
    g0: BSplineCurve PolesCount=4 KnotsCount=2 Degree=3 IsPeriodic=0
    g1: BSplineCurve PolesCount=4 KnotsCount=2 Degree=3 IsPeriodic=0
    g2: BSplineCurve PolesCount=4 KnotsCount=2 Degree=3 IsPeriodic=0
  constraints (2):
    c: Coincident(g0,g1)
    c: Coincident(g1,g2)
FEATURE [Sketcher::SketchObject] Sketch205
  sketch-geometry (2):
    g0: BSplineCurve PolesCount=4 KnotsCount=2 Degree=3 IsPeriodic=0
    g1: BSplineCurve PolesCount=4 KnotsCount=2 Degree=3 IsPeriodic=0
  constraints (1):
    c: Coincident(g0,g1)
FEATURE [Sketcher::SketchObject] Sketch206
  sketch-geometry (1):
    g0: BSplineCurve PolesCount=4 KnotsCount=2 Degree=3 IsPeriodic=0
FEATURE [Sketcher::SketchObject] Sketch207
  sketch-geometry (2):
    g0: BSplineCurve PolesCount=4 KnotsCount=2 Degree=3 IsPeriodic=0
    g1: BSplineCurve PolesCount=4 KnotsCount=2 Degree=3 IsPeriodic=0
  constraints (1):
    c: Coincident(g0,g1)
FEATURE [Sketcher::SketchObject] Sketch208
  sketch-geometry (2):
    g0: BSplineCurve PolesCount=4 KnotsCount=2 Degree=3 IsPeriodic=0
    g1: BSplineCurve PolesCount=4 KnotsCount=2 Degree=3 IsPeriodic=0
  constraints (1):
    c: Coincident(g0,g1)
FEATURE [Sketcher::SketchObject] Sketch209
  sketch-geometry (3):
    g0: BSplineCurve PolesCount=4 KnotsCount=2 Degree=3 IsPeriodic=0
    g1: BSplineCurve PolesCount=4 KnotsCount=2 Degree=3 IsPeriodic=0
    g2: BSplineCurve PolesCount=4 KnotsCount=2 Degree=3 IsPeriodic=0
  constraints (2):
    c: Coincident(g0,g1)
    c: Coincident(g1,g2)
FEATURE [Sketcher::SketchObject] Sketch210
  sketch-geometry (1):
    g0: BSplineCurve PolesCount=4 KnotsCount=2 Degree=3 IsPeriodic=0
FEATURE [Sketcher::SketchObject] Sketch211
  sketch-geometry (3):
    g0: BSplineCurve PolesCount=4 KnotsCount=2 Degree=3 IsPeriodic=0
    g1: BSplineCurve PolesCount=4 KnotsCount=2 Degree=3 IsPeriodic=0
    g2: BSplineCurve PolesCount=4 KnotsCount=2 Degree=3 IsPeriodic=0
  constraints (2):
    c: Coincident(g0,g1)
    c: Coincident(g1,g2)
FEATURE [Sketcher::SketchObject] Sketch212
  sketch-geometry (1):
    g0: BSplineCurve PolesCount=4 KnotsCount=2 Degree=3 IsPeriodic=0
FEATURE [Sketcher::SketchObject] Sketch213
  sketch-geometry (1):
    g0: BSplineCurve PolesCount=4 KnotsCount=2 Degree=3 IsPeriodic=0
FEATURE [Sketcher::SketchObject] Sketch214
  sketch-geometry (2):
    g0: BSplineCurve PolesCount=4 KnotsCount=2 Degree=3 IsPeriodic=0
    g1: BSplineCurve PolesCount=4 KnotsCount=2 Degree=3 IsPeriodic=0
  constraints (1):
    c: Coincident(g0,g1)
FEATURE [Sketcher::SketchObject] Sketch215
  sketch-geometry (1):
    g0: BSplineCurve PolesCount=4 KnotsCount=2 Degree=3 IsPeriodic=0
FEATURE [Sketcher::SketchObject] Sketch216
  sketch-geometry (1):
    g0: BSplineCurve PolesCount=4 KnotsCount=2 Degree=3 IsPeriodic=0
FEATURE [Sketcher::SketchObject] Sketch217
  sketch-geometry (2):
    g0: BSplineCurve PolesCount=4 KnotsCount=2 Degree=3 IsPeriodic=0
    g1: BSplineCurve PolesCount=4 KnotsCount=2 Degree=3 IsPeriodic=0
  constraints (1):
    c: Coincident(g0,g1)
FEATURE [Sketcher::SketchObject] Sketch218
  sketch-geometry (3):
    g0: BSplineCurve PolesCount=4 KnotsCount=2 Degree=3 IsPeriodic=0
    g1: BSplineCurve PolesCount=4 KnotsCount=2 Degree=3 IsPeriodic=0
    g2: BSplineCurve PolesCount=4 KnotsCount=2 Degree=3 IsPeriodic=0
  constraints (2):
    c: Coincident(g0,g1)
    c: Coincident(g1,g2)
FEATURE [Sketcher::SketchObject] Sketch219
  sketch-geometry (1):
    g0: BSplineCurve PolesCount=4 KnotsCount=2 Degree=3 IsPeriodic=0
FEATURE [Sketcher::SketchObject] Sketch220
  sketch-geometry (3):
    g0: BSplineCurve PolesCount=4 KnotsCount=2 Degree=3 IsPeriodic=0
    g1: BSplineCurve PolesCount=4 KnotsCount=2 Degree=3 IsPeriodic=0
    g2: BSplineCurve PolesCount=4 KnotsCount=2 Degree=3 IsPeriodic=0
  constraints (2):
    c: Coincident(g0,g1)
    c: Coincident(g1,g2)
FEATURE [Sketcher::SketchObject] Sketch221
  sketch-geometry (1):
    g0: BSplineCurve PolesCount=4 KnotsCount=2 Degree=3 IsPeriodic=0
FEATURE [Sketcher::SketchObject] Sketch222
  sketch-geometry (3):
    g0: BSplineCurve PolesCount=4 KnotsCount=2 Degree=3 IsPeriodic=0
    g1: BSplineCurve PolesCount=4 KnotsCount=2 Degree=3 IsPeriodic=0
    g2: BSplineCurve PolesCount=4 KnotsCount=2 Degree=3 IsPeriodic=0
  constraints (2):
    c: Coincident(g0,g1)
    c: Coincident(g1,g2)
FEATURE [Sketcher::SketchObject] Sketch223
  sketch-geometry (3):
    g0: BSplineCurve PolesCount=4 KnotsCount=2 Degree=3 IsPeriodic=0
    g1: BSplineCurve PolesCount=4 KnotsCount=2 Degree=3 IsPeriodic=0
    g2: BSplineCurve PolesCount=4 KnotsCount=2 Degree=3 IsPeriodic=0
  constraints (2):
    c: Coincident(g0,g1)
    c: Coincident(g1,g2)
FEATURE [Sketcher::SketchObject] Sketch224
  sketch-geometry (1):
    g0: BSplineCurve PolesCount=4 KnotsCount=2 Degree=3 IsPeriodic=0
FEATURE [Sketcher::SketchObject] Sketch225
  sketch-geometry (1):
    g0: BSplineCurve PolesCount=4 KnotsCount=2 Degree=3 IsPeriodic=0
FEATURE [Sketcher::SketchObject] Sketch226
  sketch-geometry (2):
    g0: BSplineCurve PolesCount=4 KnotsCount=2 Degree=3 IsPeriodic=0
    g1: BSplineCurve PolesCount=4 KnotsCount=2 Degree=3 IsPeriodic=0
  constraints (1):
    c: Coincident(g0,g1)
FEATURE [Sketcher::SketchObject] Sketch227
  sketch-geometry (3):
    g0: BSplineCurve PolesCount=4 KnotsCount=2 Degree=3 IsPeriodic=0
    g1: BSplineCurve PolesCount=4 KnotsCount=2 Degree=3 IsPeriodic=0
    g2: BSplineCurve PolesCount=4 KnotsCount=2 Degree=3 IsPeriodic=0
  constraints (2):
    c: Coincident(g0,g1)
    c: Coincident(g1,g2)
FEATURE [Sketcher::SketchObject] Sketch228
  sketch-geometry (1):
    g0: BSplineCurve PolesCount=4 KnotsCount=2 Degree=3 IsPeriodic=0
FEATURE [Sketcher::SketchObject] Sketch229
  sketch-geometry (3):
    g0: BSplineCurve PolesCount=4 KnotsCount=2 Degree=3 IsPeriodic=0
    g1: BSplineCurve PolesCount=4 KnotsCount=2 Degree=3 IsPeriodic=0
    g2: BSplineCurve PolesCount=4 KnotsCount=2 Degree=3 IsPeriodic=0
  constraints (2):
    c: Coincident(g0,g1)
    c: Coincident(g1,g2)
FEATURE [Sketcher::SketchObject] Sketch230
  sketch-geometry (1):
    g0: BSplineCurve PolesCount=4 KnotsCount=2 Degree=3 IsPeriodic=0
FEATURE [Sketcher::SketchObject] Sketch231
  sketch-geometry (2):
    g0: BSplineCurve PolesCount=4 KnotsCount=2 Degree=3 IsPeriodic=0
    g1: BSplineCurve PolesCount=4 KnotsCount=2 Degree=3 IsPeriodic=0
  constraints (1):
    c: Coincident(g0,g1)
FEATURE [Sketcher::SketchObject] Sketch232
  sketch-geometry (2):
    g0: BSplineCurve PolesCount=4 KnotsCount=2 Degree=3 IsPeriodic=0
    g1: BSplineCurve PolesCount=4 KnotsCount=2 Degree=3 IsPeriodic=0
  constraints (1):
    c: Coincident(g0,g1)
FEATURE [Sketcher::SketchObject] Sketch233
  sketch-geometry (1):
    g0: BSplineCurve PolesCount=4 KnotsCount=2 Degree=3 IsPeriodic=0
FEATURE [Sketcher::SketchObject] Sketch234
  sketch-geometry (1):
    g0: BSplineCurve PolesCount=4 KnotsCount=2 Degree=3 IsPeriodic=0
FEATURE [Sketcher::SketchObject] Sketch235
  sketch-geometry (2):
    g0: BSplineCurve PolesCount=4 KnotsCount=2 Degree=3 IsPeriodic=0
    g1: BSplineCurve PolesCount=4 KnotsCount=2 Degree=3 IsPeriodic=0
  constraints (1):
    c: Coincident(g0,g1)
FEATURE [Sketcher::SketchObject] Sketch236
  sketch-geometry (3):
    g0: BSplineCurve PolesCount=4 KnotsCount=2 Degree=3 IsPeriodic=0
    g1: BSplineCurve PolesCount=4 KnotsCount=2 Degree=3 IsPeriodic=0
    g2: BSplineCurve PolesCount=4 KnotsCount=2 Degree=3 IsPeriodic=0
  constraints (2):
    c: Coincident(g0,g1)
    c: Coincident(g1,g2)
FEATURE [Sketcher::SketchObject] Sketch237
  sketch-geometry (1):
    g0: BSplineCurve PolesCount=4 KnotsCount=2 Degree=3 IsPeriodic=0
FEATURE [Sketcher::SketchObject] Sketch238
  sketch-geometry (3):
    g0: BSplineCurve PolesCount=4 KnotsCount=2 Degree=3 IsPeriodic=0
    g1: BSplineCurve PolesCount=4 KnotsCount=2 Degree=3 IsPeriodic=0
    g2: BSplineCurve PolesCount=4 KnotsCount=2 Degree=3 IsPeriodic=0
  constraints (2):
    c: Coincident(g0,g1)
    c: Coincident(g1,g2)
FEATURE [Sketcher::SketchObject] Sketch239
  sketch-geometry (3):
    g0: BSplineCurve PolesCount=4 KnotsCount=2 Degree=3 IsPeriodic=0
    g1: BSplineCurve PolesCount=4 KnotsCount=2 Degree=3 IsPeriodic=0
    g2: BSplineCurve PolesCount=4 KnotsCount=2 Degree=3 IsPeriodic=0
  constraints (2):
    c: Coincident(g0,g1)
    c: Coincident(g1,g2)
FEATURE [Sketcher::SketchObject] Sketch240
  sketch-geometry (1):
    g0: BSplineCurve PolesCount=4 KnotsCount=2 Degree=3 IsPeriodic=0
FEATURE [Sketcher::SketchObject] Sketch241
  sketch-geometry (2):
    g0: BSplineCurve PolesCount=4 KnotsCount=2 Degree=3 IsPeriodic=0
    g1: BSplineCurve PolesCount=4 KnotsCount=2 Degree=3 IsPeriodic=0
  constraints (1):
    c: Coincident(g0,g1)
FEATURE [Sketcher::SketchObject] Sketch242
  sketch-geometry (1):
    g0: BSplineCurve PolesCount=4 KnotsCount=2 Degree=3 IsPeriodic=0
FEATURE [App::DocumentObjectGroup] Group  label="sketches"
  Group = -> [Sketch,Sketch001,Sketch002,Sketch003,Sketch004,Sketch005,Sketch006,Sketch007,Sketch008,Sketch009,Sketch010,Sketch011,Sketch012,Sketch013,Sketch014,Sketch015,Sketch016,Sketch017,Sketch018,Sketch019,Sketch020,Sketch021,Sketch022,Sketch023,Sketch024,Sketch025,Sketch026,Sketch027,Sketch028,Sketch029,Sketch030,Sketch031,Sketch032,Sketch033,Sketch034,Sketch035,Sketch036,Sketch037,Sketch038,Sketch039,+203 more]
FEATURE [App::DocumentObjectGroup] Group001  label="paths"
  Group = -> [path1691,path1691001,path1691002,path1691003,path1691004,path1691005,path1691006,path1691007,path1691008,path1691009,path1691010,path1691011,path1691012,path1691013,path1691014,path1691015,path1691016,path1691017,path1691018,path1691019,path1691020,path1691021,path1691022,path1691023,path1691024,path1691025,path1691026,path1691027,path1691028,path1691029,path1691030,path1691031,path1691032,+210 more]
FEATURE [Sketcher::SketchObject] Sketch243  label="pattern_front"
  Placement = pos=(-50,50,0) rot=(0,0,1;0rad)
  sketch-geometry (473):
    g0: BSplineCurve PolesCount=4 KnotsCount=2 Degree=3 IsPeriodic=0
    g1: BSplineCurve PolesCount=4 KnotsCount=2 Degree=3 IsPeriodic=0
    g2: BSplineCurve PolesCount=4 KnotsCount=2 Degree=3 IsPeriodic=0
    g3: BSplineCurve PolesCount=4 KnotsCount=2 Degree=3 IsPeriodic=0
    g4: BSplineCurve PolesCount=4 KnotsCount=2 Degree=3 IsPeriodic=0
    g5: BSplineCurve PolesCount=4 KnotsCount=2 Degree=3 IsPeriodic=0
    g6: BSplineCurve PolesCount=4 KnotsCount=2 Degree=3 IsPeriodic=0
    g7: BSplineCurve PolesCount=4 KnotsCount=2 Degree=3 IsPeriodic=0
    g8: BSplineCurve PolesCount=4 KnotsCount=2 Degree=3 IsPeriodic=0
    g9: BSplineCurve PolesCount=4 KnotsCount=2 Degree=3 IsPeriodic=0
    g10: BSplineCurve PolesCount=4 KnotsCount=2 Degree=3 IsPeriodic=0
    g11: BSplineCurve PolesCount=4 KnotsCount=2 Degree=3 IsPeriodic=0
    g12: BSplineCurve PolesCount=4 KnotsCount=2 Degree=3 IsPeriodic=0
    g13: BSplineCurve PolesCount=4 KnotsCount=2 Degree=3 IsPeriodic=0
    g14: BSplineCurve PolesCount=4 KnotsCount=2 Degree=3 IsPeriodic=0
    g15: BSplineCurve PolesCount=4 KnotsCount=2 Degree=3 IsPeriodic=0
    g16: BSplineCurve PolesCount=4 KnotsCount=2 Degree=3 IsPeriodic=0
    g17: BSplineCurve PolesCount=4 KnotsCount=2 Degree=3 IsPeriodic=0
    g18: BSplineCurve PolesCount=4 KnotsCount=2 Degree=3 IsPeriodic=0
    g19: BSplineCurve PolesCount=4 KnotsCount=2 Degree=3 IsPeriodic=0
    g20: BSplineCurve PolesCount=4 KnotsCount=2 Degree=3 IsPeriodic=0
    g21: BSplineCurve PolesCount=4 KnotsCount=2 Degree=3 IsPeriodic=0
    g22: BSplineCurve PolesCount=4 KnotsCount=2 Degree=3 IsPeriodic=0
    g23: BSplineCurve PolesCount=4 KnotsCount=2 Degree=3 IsPeriodic=0
    g24: BSplineCurve PolesCount=4 KnotsCount=2 Degree=3 IsPeriodic=0
    g25: BSplineCurve PolesCount=4 KnotsCount=2 Degree=3 IsPeriodic=0
    g26: BSplineCurve PolesCount=4 KnotsCount=2 Degree=3 IsPeriodic=0
    g27: BSplineCurve PolesCount=4 KnotsCount=2 Degree=3 IsPeriodic=0
    g28: BSplineCurve PolesCount=4 KnotsCount=2 Degree=3 IsPeriodic=0
    g29: BSplineCurve PolesCount=4 KnotsCount=2 Degree=3 IsPeriodic=0
    g30: BSplineCurve PolesCount=4 KnotsCount=2 Degree=3 IsPeriodic=0
    g31: BSplineCurve PolesCount=4 KnotsCount=2 Degree=3 IsPeriodic=0
    g32: BSplineCurve PolesCount=4 KnotsCount=2 Degree=3 IsPeriodic=0
    g33: BSplineCurve PolesCount=4 KnotsCount=2 Degree=3 IsPeriodic=0
    g34: BSplineCurve PolesCount=4 KnotsCount=2 Degree=3 IsPeriodic=0
    g35: BSplineCurve PolesCount=4 KnotsCount=2 Degree=3 IsPeriodic=0
    g36: BSplineCurve PolesCount=4 KnotsCount=2 Degree=3 IsPeriodic=0
    g37: BSplineCurve PolesCount=4 KnotsCount=2 Degree=3 IsPeriodic=0
    g38: BSplineCurve PolesCount=4 KnotsCount=2 Degree=3 IsPeriodic=0
    g39: BSplineCurve PolesCount=4 KnotsCount=2 Degree=3 IsPeriodic=0
    g40: BSplineCurve PolesCount=4 KnotsCount=2 Degree=3 IsPeriodic=0
    g41: BSplineCurve PolesCount=4 KnotsCount=2 Degree=3 IsPeriodic=0
    g42: BSplineCurve PolesCount=4 KnotsCount=2 Degree=3 IsPeriodic=0
    g43: BSplineCurve PolesCount=4 KnotsCount=2 Degree=3 IsPeriodic=0
    g44: BSplineCurve PolesCount=4 KnotsCount=2 Degree=3 IsPeriodic=0
    g45: BSplineCurve PolesCount=4 KnotsCount=2 Degree=3 IsPeriodic=0
    g46: BSplineCurve PolesCount=4 KnotsCount=2 Degree=3 IsPeriodic=0
    g47: BSplineCurve PolesCount=4 KnotsCount=2 Degree=3 IsPeriodic=0
    g48: BSplineCurve PolesCount=4 KnotsCount=2 Degree=3 IsPeriodic=0
    g49: BSplineCurve PolesCount=4 KnotsCount=2 Degree=3 IsPeriodic=0
    g50: BSplineCurve PolesCount=4 KnotsCount=2 Degree=3 IsPeriodic=0
    g51: BSplineCurve PolesCount=4 KnotsCount=2 Degree=3 IsPeriodic=0
    g52: BSplineCurve PolesCount=4 KnotsCount=2 Degree=3 IsPeriodic=0
    g53: BSplineCurve PolesCount=4 KnotsCount=2 Degree=3 IsPeriodic=0
    g54: BSplineCurve PolesCount=4 KnotsCount=2 Degree=3 IsPeriodic=0
    g55: BSplineCurve PolesCount=4 KnotsCount=2 Degree=3 IsPeriodic=0
    g56: BSplineCurve PolesCount=4 KnotsCount=2 Degree=3 IsPeriodic=0
    g57: BSplineCurve PolesCount=4 KnotsCount=2 Degree=3 IsPeriodic=0
    g58: BSplineCurve PolesCount=4 KnotsCount=2 Degree=3 IsPeriodic=0
    g59: BSplineCurve PolesCount=4 KnotsCount=2 Degree=3 IsPeriodic=0
    g60: BSplineCurve PolesCount=4 KnotsCount=2 Degree=3 IsPeriodic=0
    g61: BSplineCurve PolesCount=4 KnotsCount=2 Degree=3 IsPeriodic=0
    g62: BSplineCurve PolesCount=4 KnotsCount=2 Degree=3 IsPeriodic=0
    g63: BSplineCurve PolesCount=4 KnotsCount=2 Degree=3 IsPeriodic=0
    g64: BSplineCurve PolesCount=4 KnotsCount=2 Degree=3 IsPeriodic=0
    g65: BSplineCurve PolesCount=4 KnotsCount=2 Degree=3 IsPeriodic=0
    g66: BSplineCurve PolesCount=4 KnotsCount=2 Degree=3 IsPeriodic=0
    g67: BSplineCurve PolesCount=4 KnotsCount=2 Degree=3 IsPeriodic=0
    g68: BSplineCurve PolesCount=4 KnotsCount=2 Degree=3 IsPeriodic=0
    g69: BSplineCurve PolesCount=4 KnotsCount=2 Degree=3 IsPeriodic=0
    g70: BSplineCurve PolesCount=4 KnotsCount=2 Degree=3 IsPeriodic=0
    g71: BSplineCurve PolesCount=4 KnotsCount=2 Degree=3 IsPeriodic=0
    g72: BSplineCurve PolesCount=4 KnotsCount=2 Degree=3 IsPeriodic=0
    g73: BSplineCurve PolesCount=4 KnotsCount=2 Degree=3 IsPeriodic=0
    g74: BSplineCurve PolesCount=4 KnotsCount=2 Degree=3 IsPeriodic=0
    g75: BSplineCurve PolesCount=4 KnotsCount=2 Degree=3 IsPeriodic=0
    g76: BSplineCurve PolesCount=4 KnotsCount=2 Degree=3 IsPeriodic=0
    g77: BSplineCurve PolesCount=4 KnotsCount=2 Degree=3 IsPeriodic=0
    g78: BSplineCurve PolesCount=4 KnotsCount=2 Degree=3 IsPeriodic=0
    g79: BSplineCurve PolesCount=4 KnotsCount=2 Degree=3 IsPeriodic=0
    g80: BSplineCurve PolesCount=4 KnotsCount=2 Degree=3 IsPeriodic=0
    g81: BSplineCurve PolesCount=4 KnotsCount=2 Degree=3 IsPeriodic=0
    g82: BSplineCurve PolesCount=4 KnotsCount=2 Degree=3 IsPeriodic=0
    g83: BSplineCurve PolesCount=4 KnotsCount=2 Degree=3 IsPeriodic=0
    g84: BSplineCurve PolesCount=4 KnotsCount=2 Degree=3 IsPeriodic=0
    g85: BSplineCurve PolesCount=4 KnotsCount=2 Degree=3 IsPeriodic=0
    g86: BSplineCurve PolesCount=4 KnotsCount=2 Degree=3 IsPeriodic=0
    g87: BSplineCurve PolesCount=4 KnotsCount=2 Degree=3 IsPeriodic=0
    g88: BSplineCurve PolesCount=4 KnotsCount=2 Degree=3 IsPeriodic=0
    g89: BSplineCurve PolesCount=4 KnotsCount=2 Degree=3 IsPeriodic=0
    g90: BSplineCurve PolesCount=4 KnotsCount=2 Degree=3 IsPeriodic=0
    g91: BSplineCurve PolesCount=4 KnotsCount=2 Degree=3 IsPeriodic=0
    g92: BSplineCurve PolesCount=4 KnotsCount=2 Degree=3 IsPeriodic=0
    g93: BSplineCurve PolesCount=4 KnotsCount=2 Degree=3 IsPeriodic=0
    g94: BSplineCurve PolesCount=4 KnotsCount=2 Degree=3 IsPeriodic=0
    g95: BSplineCurve PolesCount=4 KnotsCount=2 Degree=3 IsPeriodic=0
    g96: BSplineCurve PolesCount=4 KnotsCount=2 Degree=3 IsPeriodic=0
    g97: BSplineCurve PolesCount=4 KnotsCount=2 Degree=3 IsPeriodic=0
    g98: BSplineCurve PolesCount=4 KnotsCount=2 Degree=3 IsPeriodic=0
    g99: BSplineCurve PolesCount=4 KnotsCount=2 Degree=3 IsPeriodic=0
    g100: BSplineCurve PolesCount=4 KnotsCount=2 Degree=3 IsPeriodic=0
    g101: BSplineCurve PolesCount=4 KnotsCount=2 Degree=3 IsPeriodic=0
    g102: BSplineCurve PolesCount=4 KnotsCount=2 Degree=3 IsPeriodic=0
    g103: BSplineCurve PolesCount=4 KnotsCount=2 Degree=3 IsPeriodic=0
    g104: BSplineCurve PolesCount=4 KnotsCount=2 Degree=3 IsPeriodic=0
    g105: BSplineCurve PolesCount=4 KnotsCount=2 Degree=3 IsPeriodic=0
    g106: BSplineCurve PolesCount=4 KnotsCount=2 Degree=3 IsPeriodic=0
    g107: BSplineCurve PolesCount=4 KnotsCount=2 Degree=3 IsPeriodic=0
    g108: BSplineCurve PolesCount=4 KnotsCount=2 Degree=3 IsPeriodic=0
    g109: BSplineCurve PolesCount=4 KnotsCount=2 Degree=3 IsPeriodic=0
    g110: BSplineCurve PolesCount=4 KnotsCount=2 Degree=3 IsPeriodic=0
    g111: BSplineCurve PolesCount=4 KnotsCount=2 Degree=3 IsPeriodic=0
    g112: BSplineCurve PolesCount=4 KnotsCount=2 Degree=3 IsPeriodic=0
    g113: BSplineCurve PolesCount=4 KnotsCount=2 Degree=3 IsPeriodic=0
    g114: BSplineCurve PolesCount=4 KnotsCount=2 Degree=3 IsPeriodic=0
    g115: BSplineCurve PolesCount=4 KnotsCount=2 Degree=3 IsPeriodic=0
    g116: BSplineCurve PolesCount=4 KnotsCount=2 Degree=3 IsPeriodic=0
    g117: BSplineCurve PolesCount=4 KnotsCount=2 Degree=3 IsPeriodic=0
    g118: BSplineCurve PolesCount=4 KnotsCount=2 Degree=3 IsPeriodic=0
    g119: BSplineCurve PolesCount=4 KnotsCount=2 Degree=3 IsPeriodic=0
    g120: BSplineCurve PolesCount=4 KnotsCount=2 Degree=3 IsPeriodic=0
    g121: BSplineCurve PolesCount=4 KnotsCount=2 Degree=3 IsPeriodic=0
    g122: BSplineCurve PolesCount=4 KnotsCount=2 Degree=3 IsPeriodic=0
    g123: BSplineCurve PolesCount=4 KnotsCount=2 Degree=3 IsPeriodic=0
    g124: BSplineCurve PolesCount=4 KnotsCount=2 Degree=3 IsPeriodic=0
    g125: BSplineCurve PolesCount=4 KnotsCount=2 Degree=3 IsPeriodic=0
    g126: BSplineCurve PolesCount=4 KnotsCount=2 Degree=3 IsPeriodic=0
    g127: BSplineCurve PolesCount=4 KnotsCount=2 Degree=3 IsPeriodic=0
    g128: BSplineCurve PolesCount=4 KnotsCount=2 Degree=3 IsPeriodic=0
    g129: BSplineCurve PolesCount=4 KnotsCount=2 Degree=3 IsPeriodic=0
    g130: BSplineCurve PolesCount=4 KnotsCount=2 Degree=3 IsPeriodic=0
    g131: BSplineCurve PolesCount=4 KnotsCount=2 Degree=3 IsPeriodic=0
    g132: BSplineCurve PolesCount=4 KnotsCount=2 Degree=3 IsPeriodic=0
    g133: BSplineCurve PolesCount=4 KnotsCount=2 Degree=3 IsPeriodic=0
    g134: BSplineCurve PolesCount=4 KnotsCount=2 Degree=3 IsPeriodic=0
    g135: BSplineCurve PolesCount=4 KnotsCount=2 Degree=3 IsPeriodic=0
    g136: BSplineCurve PolesCount=4 KnotsCount=2 Degree=3 IsPeriodic=0
    g137: BSplineCurve PolesCount=4 KnotsCount=2 Degree=3 IsPeriodic=0
    g138: BSplineCurve PolesCount=4 KnotsCount=2 Degree=3 IsPeriodic=0
    g139: BSplineCurve PolesCount=4 KnotsCount=2 Degree=3 IsPeriodic=0
    g140: BSplineCurve PolesCount=4 KnotsCount=2 Degree=3 IsPeriodic=0
    g141: BSplineCurve PolesCount=4 KnotsCount=2 Degree=3 IsPeriodic=0
    g142: BSplineCurve PolesCount=4 KnotsCount=2 Degree=3 IsPeriodic=0
    g143: BSplineCurve PolesCount=4 KnotsCount=2 Degree=3 IsPeriodic=0
    g144: BSplineCurve PolesCount=4 KnotsCount=2 Degree=3 IsPeriodic=0
    g145: BSplineCurve PolesCount=4 KnotsCount=2 Degree=3 IsPeriodic=0
    g146: BSplineCurve PolesCount=4 KnotsCount=2 Degree=3 IsPeriodic=0
    g147: BSplineCurve PolesCount=4 KnotsCount=2 Degree=3 IsPeriodic=0
    g148: BSplineCurve PolesCount=4 KnotsCount=2 Degree=3 IsPeriodic=0
    g149: BSplineCurve PolesCount=4 KnotsCount=2 Degree=3 IsPeriodic=0
    g150: BSplineCurve PolesCount=4 KnotsCount=2 Degree=3 IsPeriodic=0
    g151: BSplineCurve PolesCount=4 KnotsCount=2 Degree=3 IsPeriodic=0
    g152: BSplineCurve PolesCount=4 KnotsCount=2 Degree=3 IsPeriodic=0
    g153: BSplineCurve PolesCount=4 KnotsCount=2 Degree=3 IsPeriodic=0
    g154: BSplineCurve PolesCount=4 KnotsCount=2 Degree=3 IsPeriodic=0
    g155: BSplineCurve PolesCount=4 KnotsCount=2 Degree=3 IsPeriodic=0
    g156: BSplineCurve PolesCount=4 KnotsCount=2 Degree=3 IsPeriodic=0
    g157: BSplineCurve PolesCount=4 KnotsCount=2 Degree=3 IsPeriodic=0
    g158: BSplineCurve PolesCount=4 KnotsCount=2 Degree=3 IsPeriodic=0
    g159: BSplineCurve PolesCount=4 KnotsCount=2 Degree=3 IsPeriodic=0
    g160: BSplineCurve PolesCount=4 KnotsCount=2 Degree=3 IsPeriodic=0
    g161: BSplineCurve PolesCount=4 KnotsCount=2 Degree=3 IsPeriodic=0
    g162: BSplineCurve PolesCount=4 KnotsCount=2 Degree=3 IsPeriodic=0
    g163: BSplineCurve PolesCount=4 KnotsCount=2 Degree=3 IsPeriodic=0
    g164: BSplineCurve PolesCount=4 KnotsCount=2 Degree=3 IsPeriodic=0
    g165: BSplineCurve PolesCount=4 KnotsCount=2 Degree=3 IsPeriodic=0
    g166: BSplineCurve PolesCount=4 KnotsCount=2 Degree=3 IsPeriodic=0
    g167: BSplineCurve PolesCount=4 KnotsCount=2 Degree=3 IsPeriodic=0
    g168: BSplineCurve PolesCount=4 KnotsCount=2 Degree=3 IsPeriodic=0
    g169: BSplineCurve PolesCount=4 KnotsCount=2 Degree=3 IsPeriodic=0
    g170: BSplineCurve PolesCount=4 KnotsCount=2 Degree=3 IsPeriodic=0
    g171: BSplineCurve PolesCount=4 KnotsCount=2 Degree=3 IsPeriodic=0
    g172: BSplineCurve PolesCount=4 KnotsCount=2 Degree=3 IsPeriodic=0
    g173: BSplineCurve PolesCount=4 KnotsCount=2 Degree=3 IsPeriodic=0
    g174: BSplineCurve PolesCount=4 KnotsCount=2 Degree=3 IsPeriodic=0
    g175: BSplineCurve PolesCount=4 KnotsCount=2 Degree=3 IsPeriodic=0
    g176: BSplineCurve PolesCount=4 KnotsCount=2 Degree=3 IsPeriodic=0
    g177: BSplineCurve PolesCount=4 KnotsCount=2 Degree=3 IsPeriodic=0
    g178: BSplineCurve PolesCount=4 KnotsCount=2 Degree=3 IsPeriodic=0
    g179: BSplineCurve PolesCount=4 KnotsCount=2 Degree=3 IsPeriodic=0
    g180: BSplineCurve PolesCount=4 KnotsCount=2 Degree=3 IsPeriodic=0
    g181: BSplineCurve PolesCount=4 KnotsCount=2 Degree=3 IsPeriodic=0
    g182: BSplineCurve PolesCount=4 KnotsCount=2 Degree=3 IsPeriodic=0
    g183: BSplineCurve PolesCount=4 KnotsCount=2 Degree=3 IsPeriodic=0
    g184: BSplineCurve PolesCount=4 KnotsCount=2 Degree=3 IsPeriodic=0
    g185: BSplineCurve PolesCount=4 KnotsCount=2 Degree=3 IsPeriodic=0
    g186: BSplineCurve PolesCount=4 KnotsCount=2 Degree=3 IsPeriodic=0
    g187: BSplineCurve PolesCount=4 KnotsCount=2 Degree=3 IsPeriodic=0
    g188: BSplineCurve PolesCount=4 KnotsCount=2 Degree=3 IsPeriodic=0
    g189: BSplineCurve PolesCount=4 KnotsCount=2 Degree=3 IsPeriodic=0
    g190: BSplineCurve PolesCount=4 KnotsCount=2 Degree=3 IsPeriodic=0
    g191: BSplineCurve PolesCount=4 KnotsCount=2 Degree=3 IsPeriodic=0
    g192: BSplineCurve PolesCount=4 KnotsCount=2 Degree=3 IsPeriodic=0
    g193: BSplineCurve PolesCount=4 KnotsCount=2 Degree=3 IsPeriodic=0
    g194: BSplineCurve PolesCount=4 KnotsCount=2 Degree=3 IsPeriodic=0
    g195: BSplineCurve PolesCount=4 KnotsCount=2 Degree=3 IsPeriodic=0
    g196: BSplineCurve PolesCount=4 KnotsCount=2 Degree=3 IsPeriodic=0
    g197: BSplineCurve PolesCount=4 KnotsCount=2 Degree=3 IsPeriodic=0
    g198: BSplineCurve PolesCount=4 KnotsCount=2 Degree=3 IsPeriodic=0
    g199: BSplineCurve PolesCount=4 KnotsCount=2 Degree=3 IsPeriodic=0
    g200: BSplineCurve PolesCount=4 KnotsCount=2 Degree=3 IsPeriodic=0
    g201: BSplineCurve PolesCount=4 KnotsCount=2 Degree=3 IsPeriodic=0
    g202: BSplineCurve PolesCount=4 KnotsCount=2 Degree=3 IsPeriodic=0
    g203: BSplineCurve PolesCount=4 KnotsCount=2 Degree=3 IsPeriodic=0
    g204: BSplineCurve PolesCount=4 KnotsCount=2 Degree=3 IsPeriodic=0
    g205: BSplineCurve PolesCount=4 KnotsCount=2 Degree=3 IsPeriodic=0
    g206: BSplineCurve PolesCount=4 KnotsCount=2 Degree=3 IsPeriodic=0
    g207: BSplineCurve PolesCount=4 KnotsCount=2 Degree=3 IsPeriodic=0
    g208: BSplineCurve PolesCount=4 KnotsCount=2 Degree=3 IsPeriodic=0
    g209: BSplineCurve PolesCount=4 KnotsCount=2 Degree=3 IsPeriodic=0
    g210: BSplineCurve PolesCount=4 KnotsCount=2 Degree=3 IsPeriodic=0
    g211: BSplineCurve PolesCount=4 KnotsCount=2 Degree=3 IsPeriodic=0
    g212: BSplineCurve PolesCount=4 KnotsCount=2 Degree=3 IsPeriodic=0
    g213: BSplineCurve PolesCount=4 KnotsCount=2 Degree=3 IsPeriodic=0
    g214: BSplineCurve PolesCount=4 KnotsCount=2 Degree=3 IsPeriodic=0
    g215: BSplineCurve PolesCount=4 KnotsCount=2 Degree=3 IsPeriodic=0
    g216: BSplineCurve PolesCount=4 KnotsCount=2 Degree=3 IsPeriodic=0
    g217: BSplineCurve PolesCount=4 KnotsCount=2 Degree=3 IsPeriodic=0
    g218: BSplineCurve PolesCount=4 KnotsCount=2 Degree=3 IsPeriodic=0
    g219: BSplineCurve PolesCount=4 KnotsCount=2 Degree=3 IsPeriodic=0
    g220: BSplineCurve PolesCount=4 KnotsCount=2 Degree=3 IsPeriodic=0
    g221: BSplineCurve PolesCount=4 KnotsCount=2 Degree=3 IsPeriodic=0
    g222: BSplineCurve PolesCount=4 KnotsCount=2 Degree=3 IsPeriodic=0
    g223: BSplineCurve PolesCount=4 KnotsCount=2 Degree=3 IsPeriodic=0
    g224: BSplineCurve PolesCount=4 KnotsCount=2 Degree=3 IsPeriodic=0
    g225: BSplineCurve PolesCount=4 KnotsCount=2 Degree=3 IsPeriodic=0
    g226: BSplineCurve PolesCount=4 KnotsCount=2 Degree=3 IsPeriodic=0
    g227: BSplineCurve PolesCount=4 KnotsCount=2 Degree=3 IsPeriodic=0
    g228: BSplineCurve PolesCount=4 KnotsCount=2 Degree=3 IsPeriodic=0
    g229: BSplineCurve PolesCount=4 KnotsCount=2 Degree=3 IsPeriodic=0
    g230: BSplineCurve PolesCount=4 KnotsCount=2 Degree=3 IsPeriodic=0
    g231: BSplineCurve PolesCount=4 KnotsCount=2 Degree=3 IsPeriodic=0
    g232: BSplineCurve PolesCount=4 KnotsCount=2 Degree=3 IsPeriodic=0
    g233: BSplineCurve PolesCount=4 KnotsCount=2 Degree=3 IsPeriodic=0
    g234: BSplineCurve PolesCount=4 KnotsCount=2 Degree=3 IsPeriodic=0
    g235: BSplineCurve PolesCount=4 KnotsCount=2 Degree=3 IsPeriodic=0
    g236: BSplineCurve PolesCount=4 KnotsCount=2 Degree=3 IsPeriodic=0
    g237: BSplineCurve PolesCount=4 KnotsCount=2 Degree=3 IsPeriodic=0
    g238: BSplineCurve PolesCount=4 KnotsCount=2 Degree=3 IsPeriodic=0
    g239: BSplineCurve PolesCount=4 KnotsCount=2 Degree=3 IsPeriodic=0
    g240: BSplineCurve PolesCount=4 KnotsCount=2 Degree=3 IsPeriodic=0
    g241: BSplineCurve PolesCount=4 KnotsCount=2 Degree=3 IsPeriodic=0
    g242: BSplineCurve PolesCount=4 KnotsCount=2 Degree=3 IsPeriodic=0
    g243: BSplineCurve PolesCount=4 KnotsCount=2 Degree=3 IsPeriodic=0
    g244: BSplineCurve PolesCount=4 KnotsCount=2 Degree=3 IsPeriodic=0
    g245: BSplineCurve PolesCount=4 KnotsCount=2 Degree=3 IsPeriodic=0
    g246: BSplineCurve PolesCount=4 KnotsCount=2 Degree=3 IsPeriodic=0
    g247: BSplineCurve PolesCount=4 KnotsCount=2 Degree=3 IsPeriodic=0
    g248: BSplineCurve PolesCount=4 KnotsCount=2 Degree=3 IsPeriodic=0
    g249: BSplineCurve PolesCount=4 KnotsCount=2 Degree=3 IsPeriodic=0
    g250: BSplineCurve PolesCount=4 KnotsCount=2 Degree=3 IsPeriodic=0
    g251: BSplineCurve PolesCount=4 KnotsCount=2 Degree=3 IsPeriodic=0
    g252: BSplineCurve PolesCount=4 KnotsCount=2 Degree=3 IsPeriodic=0
    g253: BSplineCurve PolesCount=4 KnotsCount=2 Degree=3 IsPeriodic=0
    g254: BSplineCurve PolesCount=4 KnotsCount=2 Degree=3 IsPeriodic=0
    g255: BSplineCurve PolesCount=4 KnotsCount=2 Degree=3 IsPeriodic=0
    g256: BSplineCurve PolesCount=4 KnotsCount=2 Degree=3 IsPeriodic=0
    g257: BSplineCurve PolesCount=4 KnotsCount=2 Degree=3 IsPeriodic=0
    g258: BSplineCurve PolesCount=4 KnotsCount=2 Degree=3 IsPeriodic=0
    g259: BSplineCurve PolesCount=4 KnotsCount=2 Degree=3 IsPeriodic=0
    g260: BSplineCurve PolesCount=4 KnotsCount=2 Degree=3 IsPeriodic=0
    g261: BSplineCurve PolesCount=4 KnotsCount=2 Degree=3 IsPeriodic=0
    g262: BSplineCurve PolesCount=4 KnotsCount=2 Degree=3 IsPeriodic=0
    g263: BSplineCurve PolesCount=4 KnotsCount=2 Degree=3 IsPeriodic=0
    g264: BSplineCurve PolesCount=4 KnotsCount=2 Degree=3 IsPeriodic=0
    g265: BSplineCurve PolesCount=4 KnotsCount=2 Degree=3 IsPeriodic=0
    g266: BSplineCurve PolesCount=4 KnotsCount=2 Degree=3 IsPeriodic=0
    g267: BSplineCurve PolesCount=4 KnotsCount=2 Degree=3 IsPeriodic=0
    g268: BSplineCurve PolesCount=4 KnotsCount=2 Degree=3 IsPeriodic=0
    g269: BSplineCurve PolesCount=4 KnotsCount=2 Degree=3 IsPeriodic=0
    g270: BSplineCurve PolesCount=4 KnotsCount=2 Degree=3 IsPeriodic=0
    g271: BSplineCurve PolesCount=4 KnotsCount=2 Degree=3 IsPeriodic=0
    g272: BSplineCurve PolesCount=4 KnotsCount=2 Degree=3 IsPeriodic=0
    g273: BSplineCurve PolesCount=4 KnotsCount=2 Degree=3 IsPeriodic=0
    g274: BSplineCurve PolesCount=4 KnotsCount=2 Degree=3 IsPeriodic=0
    g275: BSplineCurve PolesCount=4 KnotsCount=2 Degree=3 IsPeriodic=0
    g276: BSplineCurve PolesCount=4 KnotsCount=2 Degree=3 IsPeriodic=0
    g277: BSplineCurve PolesCount=4 KnotsCount=2 Degree=3 IsPeriodic=0
    g278: BSplineCurve PolesCount=4 KnotsCount=2 Degree=3 IsPeriodic=0
    g279: BSplineCurve PolesCount=4 KnotsCount=2 Degree=3 IsPeriodic=0
    g280: BSplineCurve PolesCount=4 KnotsCount=2 Degree=3 IsPeriodic=0
    g281: BSplineCurve PolesCount=4 KnotsCount=2 Degree=3 IsPeriodic=0
    g282: BSplineCurve PolesCount=4 KnotsCount=2 Degree=3 IsPeriodic=0
    g283: BSplineCurve PolesCount=4 KnotsCount=2 Degree=3 IsPeriodic=0
    g284: BSplineCurve PolesCount=4 KnotsCount=2 Degree=3 IsPeriodic=0
    g285: BSplineCurve PolesCount=4 KnotsCount=2 Degree=3 IsPeriodic=0
    g286: BSplineCurve PolesCount=4 KnotsCount=2 Degree=3 IsPeriodic=0
    g287: BSplineCurve PolesCount=4 KnotsCount=2 Degree=3 IsPeriodic=0
    g288: BSplineCurve PolesCount=4 KnotsCount=2 Degree=3 IsPeriodic=0
    g289: BSplineCurve PolesCount=4 KnotsCount=2 Degree=3 IsPeriodic=0
    g290: BSplineCurve PolesCount=4 KnotsCount=2 Degree=3 IsPeriodic=0
    g291: BSplineCurve PolesCount=4 KnotsCount=2 Degree=3 IsPeriodic=0
    g292: BSplineCurve PolesCount=4 KnotsCount=2 Degree=3 IsPeriodic=0
    g293: BSplineCurve PolesCount=4 KnotsCount=2 Degree=3 IsPeriodic=0
    g294: BSplineCurve PolesCount=4 KnotsCount=2 Degree=3 IsPeriodic=0
    g295: BSplineCurve PolesCount=4 KnotsCount=2 Degree=3 IsPeriodic=0
    g296: BSplineCurve PolesCount=4 KnotsCount=2 Degree=3 IsPeriodic=0
    g297: BSplineCurve PolesCount=4 KnotsCount=2 Degree=3 IsPeriodic=0
    g298: BSplineCurve PolesCount=4 KnotsCount=2 Degree=3 IsPeriodic=0
    g299: BSplineCurve PolesCount=4 KnotsCount=2 Degree=3 IsPeriodic=0
    g300: BSplineCurve PolesCount=4 KnotsCount=2 Degree=3 IsPeriodic=0
    g301: BSplineCurve PolesCount=4 KnotsCount=2 Degree=3 IsPeriodic=0
    g302: BSplineCurve PolesCount=4 KnotsCount=2 Degree=3 IsPeriodic=0
    g303: BSplineCurve PolesCount=4 KnotsCount=2 Degree=3 IsPeriodic=0
    g304: BSplineCurve PolesCount=4 KnotsCount=2 Degree=3 IsPeriodic=0
    g305: BSplineCurve PolesCount=4 KnotsCount=2 Degree=3 IsPeriodic=0
    g306: BSplineCurve PolesCount=4 KnotsCount=2 Degree=3 IsPeriodic=0
    g307: BSplineCurve PolesCount=4 KnotsCount=2 Degree=3 IsPeriodic=0
    g308: BSplineCurve PolesCount=4 KnotsCount=2 Degree=3 IsPeriodic=0
    g309: BSplineCurve PolesCount=4 KnotsCount=2 Degree=3 IsPeriodic=0
    g310: BSplineCurve PolesCount=4 KnotsCount=2 Degree=3 IsPeriodic=0
    g311: BSplineCurve PolesCount=4 KnotsCount=2 Degree=3 IsPeriodic=0
    g312: BSplineCurve PolesCount=4 KnotsCount=2 Degree=3 IsPeriodic=0
    g313: BSplineCurve PolesCount=4 KnotsCount=2 Degree=3 IsPeriodic=0
    g314: BSplineCurve PolesCount=4 KnotsCount=2 Degree=3 IsPeriodic=0
    g315: BSplineCurve PolesCount=4 KnotsCount=2 Degree=3 IsPeriodic=0
    g316: BSplineCurve PolesCount=4 KnotsCount=2 Degree=3 IsPeriodic=0
    g317: BSplineCurve PolesCount=4 KnotsCount=2 Degree=3 IsPeriodic=0
    g318: BSplineCurve PolesCount=4 KnotsCount=2 Degree=3 IsPeriodic=0
    g319: BSplineCurve PolesCount=4 KnotsCount=2 Degree=3 IsPeriodic=0
    g320: BSplineCurve PolesCount=4 KnotsCount=2 Degree=3 IsPeriodic=0
    g321: BSplineCurve PolesCount=4 KnotsCount=2 Degree=3 IsPeriodic=0
    g322: BSplineCurve PolesCount=4 KnotsCount=2 Degree=3 IsPeriodic=0
    g323: BSplineCurve PolesCount=4 KnotsCount=2 Degree=3 IsPeriodic=0
    g324: BSplineCurve PolesCount=4 KnotsCount=2 Degree=3 IsPeriodic=0
    g325: BSplineCurve PolesCount=4 KnotsCount=2 Degree=3 IsPeriodic=0
    g326: BSplineCurve PolesCount=4 KnotsCount=2 Degree=3 IsPeriodic=0
    g327: BSplineCurve PolesCount=4 KnotsCount=2 Degree=3 IsPeriodic=0
    g328: BSplineCurve PolesCount=4 KnotsCount=2 Degree=3 IsPeriodic=0
    g329: BSplineCurve PolesCount=4 KnotsCount=2 Degree=3 IsPeriodic=0
    g330: BSplineCurve PolesCount=4 KnotsCount=2 Degree=3 IsPeriodic=0
    g331: BSplineCurve PolesCount=4 KnotsCount=2 Degree=3 IsPeriodic=0
    g332: BSplineCurve PolesCount=4 KnotsCount=2 Degree=3 IsPeriodic=0
    g333: BSplineCurve PolesCount=4 KnotsCount=2 Degree=3 IsPeriodic=0
    g334: BSplineCurve PolesCount=4 KnotsCount=2 Degree=3 IsPeriodic=0
    g335: BSplineCurve PolesCount=4 KnotsCount=2 Degree=3 IsPeriodic=0
    g336: BSplineCurve PolesCount=4 KnotsCount=2 Degree=3 IsPeriodic=0
    g337: BSplineCurve PolesCount=4 KnotsCount=2 Degree=3 IsPeriodic=0
    g338: BSplineCurve PolesCount=4 KnotsCount=2 Degree=3 IsPeriodic=0
    g339: BSplineCurve PolesCount=4 KnotsCount=2 Degree=3 IsPeriodic=0
    g340: BSplineCurve PolesCount=4 KnotsCount=2 Degree=3 IsPeriodic=0
    g341: BSplineCurve PolesCount=4 KnotsCount=2 Degree=3 IsPeriodic=0
    g342: BSplineCurve PolesCount=4 KnotsCount=2 Degree=3 IsPeriodic=0
    g343: BSplineCurve PolesCount=4 KnotsCount=2 Degree=3 IsPeriodic=0
    g344: BSplineCurve PolesCount=4 KnotsCount=2 Degree=3 IsPeriodic=0
    g345: BSplineCurve PolesCount=4 KnotsCount=2 Degree=3 IsPeriodic=0
    g346: BSplineCurve PolesCount=4 KnotsCount=2 Degree=3 IsPeriodic=0
    g347: BSplineCurve PolesCount=4 KnotsCount=2 Degree=3 IsPeriodic=0
    g348: BSplineCurve PolesCount=4 KnotsCount=2 Degree=3 IsPeriodic=0
    g349: BSplineCurve PolesCount=4 KnotsCount=2 Degree=3 IsPeriodic=0
    g350: BSplineCurve PolesCount=4 KnotsCount=2 Degree=3 IsPeriodic=0
    g351: BSplineCurve PolesCount=4 KnotsCount=2 Degree=3 IsPeriodic=0
    g352: BSplineCurve PolesCount=4 KnotsCount=2 Degree=3 IsPeriodic=0
    g353: BSplineCurve PolesCount=4 KnotsCount=2 Degree=3 IsPeriodic=0
    g354: BSplineCurve PolesCount=4 KnotsCount=2 Degree=3 IsPeriodic=0
    g355: BSplineCurve PolesCount=4 KnotsCount=2 Degree=3 IsPeriodic=0
    g356: BSplineCurve PolesCount=4 KnotsCount=2 Degree=3 IsPeriodic=0
    g357: BSplineCurve PolesCount=4 KnotsCount=2 Degree=3 IsPeriodic=0
    g358: BSplineCurve PolesCount=4 KnotsCount=2 Degree=3 IsPeriodic=0
    g359: BSplineCurve PolesCount=4 KnotsCount=2 Degree=3 IsPeriodic=0
    g360: BSplineCurve PolesCount=4 KnotsCount=2 Degree=3 IsPeriodic=0
    g361: BSplineCurve PolesCount=4 KnotsCount=2 Degree=3 IsPeriodic=0
    g362: BSplineCurve PolesCount=4 KnotsCount=2 Degree=3 IsPeriodic=0
    g363: BSplineCurve PolesCount=4 KnotsCount=2 Degree=3 IsPeriodic=0
    g364: BSplineCurve PolesCount=4 KnotsCount=2 Degree=3 IsPeriodic=0
    g365: BSplineCurve PolesCount=4 KnotsCount=2 Degree=3 IsPeriodic=0
    g366: BSplineCurve PolesCount=4 KnotsCount=2 Degree=3 IsPeriodic=0
    g367: BSplineCurve PolesCount=4 KnotsCount=2 Degree=3 IsPeriodic=0
    g368: BSplineCurve PolesCount=4 KnotsCount=2 Degree=3 IsPeriodic=0
    g369: BSplineCurve PolesCount=4 KnotsCount=2 Degree=3 IsPeriodic=0
    g370: BSplineCurve PolesCount=4 KnotsCount=2 Degree=3 IsPeriodic=0
    g371: BSplineCurve PolesCount=4 KnotsCount=2 Degree=3 IsPeriodic=0
    g372: BSplineCurve PolesCount=4 KnotsCount=2 Degree=3 IsPeriodic=0
    g373: BSplineCurve PolesCount=4 KnotsCount=2 Degree=3 IsPeriodic=0
    g374: BSplineCurve PolesCount=4 KnotsCount=2 Degree=3 IsPeriodic=0
    g375: BSplineCurve PolesCount=4 KnotsCount=2 Degree=3 IsPeriodic=0
    g376: BSplineCurve PolesCount=4 KnotsCount=2 Degree=3 IsPeriodic=0
    g377: BSplineCurve PolesCount=4 KnotsCount=2 Degree=3 IsPeriodic=0
    g378: BSplineCurve PolesCount=4 KnotsCount=2 Degree=3 IsPeriodic=0
    g379: BSplineCurve PolesCount=4 KnotsCount=2 Degree=3 IsPeriodic=0
    g380: BSplineCurve PolesCount=4 KnotsCount=2 Degree=3 IsPeriodic=0
    g381: BSplineCurve PolesCount=4 KnotsCount=2 Degree=3 IsPeriodic=0
    g382: BSplineCurve PolesCount=4 KnotsCount=2 Degree=3 IsPeriodic=0
    g383: BSplineCurve PolesCount=4 KnotsCount=2 Degree=3 IsPeriodic=0
    g384: BSplineCurve PolesCount=4 KnotsCount=2 Degree=3 IsPeriodic=0
    g385: BSplineCurve PolesCount=4 KnotsCount=2 Degree=3 IsPeriodic=0
    g386: BSplineCurve PolesCount=4 KnotsCount=2 Degree=3 IsPeriodic=0
    g387: BSplineCurve PolesCount=4 KnotsCount=2 Degree=3 IsPeriodic=0
    g388: BSplineCurve PolesCount=4 KnotsCount=2 Degree=3 IsPeriodic=0
    g389: BSplineCurve PolesCount=4 KnotsCount=2 Degree=3 IsPeriodic=0
    g390: BSplineCurve PolesCount=4 KnotsCount=2 Degree=3 IsPeriodic=0
    g391: BSplineCurve PolesCount=4 KnotsCount=2 Degree=3 IsPeriodic=0
    g392: BSplineCurve PolesCount=4 KnotsCount=2 Degree=3 IsPeriodic=0
    g393: BSplineCurve PolesCount=4 KnotsCount=2 Degree=3 IsPeriodic=0
    g394: BSplineCurve PolesCount=4 KnotsCount=2 Degree=3 IsPeriodic=0
    g395: BSplineCurve PolesCount=4 KnotsCount=2 Degree=3 IsPeriodic=0
    g396: BSplineCurve PolesCount=4 KnotsCount=2 Degree=3 IsPeriodic=0
    g397: BSplineCurve PolesCount=4 KnotsCount=2 Degree=3 IsPeriodic=0
    g398: BSplineCurve PolesCount=4 KnotsCount=2 Degree=3 IsPeriodic=0
    g399: BSplineCurve PolesCount=4 KnotsCount=2 Degree=3 IsPeriodic=0
    ... +73 more geometry lines
  constraints (230):
    c: Coincident(g1,g2)
    c: Coincident(g2,g3)
    c: Coincident(g4,g5)
    c: Coincident(g5,g6)
    c: Coincident(g8,g9)
    c: Coincident(g9,g10)
    c: Coincident(g11,g12)
    c: Coincident(g12,g13)
    c: Coincident(g15,g16)
    c: Coincident(g16,g17)
    c: Coincident(g19,g20)
    c: Coincident(g20,g21)
    c: Coincident(g22,g23)
    c: Coincident(g26,g27)
    c: Coincident(g27,g28)
    c: Coincident(g29,g30)
    c: Coincident(g32,g33)
    c: Coincident(g35,g36)
    c: Coincident(g37,g38)
    c: Coincident(g38,g39)
    c: Coincident(g41,g42)
    c: Coincident(g42,g43)
    c: Coincident(g48,g49)
    c: Coincident(g50,g51)
    c: Coincident(g51,g52)
    c: Coincident(g53,g54)
    c: Coincident(g55,g56)
    c: Coincident(g56,g57)
    c: Coincident(g58,g59)
    c: Coincident(g59,g60)
    c: Coincident(g62,g63)
    c: Coincident(g63,g64)
    c: Coincident(g67,g68)
    c: Coincident(g70,g71)
    c: Coincident(g71,g72)
    c: Coincident(g74,g75)
    c: Coincident(g75,g76)
    c: Coincident(g77,g78)
    c: Coincident(g81,g82)
    c: Coincident(g83,g84)
    c: Coincident(g84,g85)
    c: Coincident(g86,g87)
    c: Coincident(g87,g88)
    c: Coincident(g89,g90)
    c: Coincident(g90,g91)
    c: Coincident(g92,g93)
    c: Coincident(g96,g97)
    c: Coincident(g98,g99)
    c: Coincident(g99,g100)
    c: Coincident(g103,g104)
    c: Coincident(g104,g105)
    c: Coincident(g107,g108)
    c: Coincident(g108,g109)
    c: Coincident(g111,g112)
    c: Coincident(g112,g113)
    c: Coincident(g114,g115)
    c: Coincident(g115,g116)
    c: Coincident(g118,g119)
    c: Coincident(g120,g121)
    c: Coincident(g124,g125)
    c: Coincident(g125,g126)
    c: Coincident(g128,g129)
    c: Coincident(g129,g130)
    c: Coincident(g131,g132)
    c: Coincident(g132,g133)
    c: Coincident(g134,g135)
    c: Coincident(g135,g136)
    c: Coincident(g137,g138)
    c: Coincident(g138,g139)
    c: Coincident(g140,g141)
    c: Coincident(g144,g145)
    c: Coincident(g145,g146)
    c: Coincident(g147,g148)
    c: Coincident(g148,g149)
    c: Coincident(g154,g155)
    c: Coincident(g156,g157)
    c: Coincident(g157,g158)
    c: Coincident(g160,g161)
    c: Coincident(g162,g163)
    c: Coincident(g163,g164)
    c: Coincident(g165,g166)
    c: Coincident(g166,g167)
    c: Coincident(g168,g169)
    c: Coincident(g169,g170)
    c: Coincident(g172,g173)
    c: Coincident(g173,g174)
    c: Coincident(g175,g176)
    c: Coincident(g179,g180)
    c: Coincident(g183,g184)
    c: Coincident(g184,g185)
    c: Coincident(g187,g188)
    c: Coincident(g188,g189)
    c: Coincident(g190,g191)
    c: Coincident(g194,g195)
    c: Coincident(g195,g196)
    c: Coincident(g197,g198)
    c: Coincident(g198,g199)
    c: Coincident(g201,g202)
    c: Coincident(g202,g203)
    c: Coincident(g206,g207)
    c: Coincident(g208,g209)
    c: Coincident(g209,g210)
    c: Coincident(g211,g212)
    c: Coincident(g213,g214)
    c: Coincident(g214,g215)
    c: Coincident(g216,g217)
    c: Coincident(g217,g218)
    c: Coincident(g220,g221)
    c: Coincident(g221,g222)
    c: Coincident(g222,g223)
    c: Coincident(g225,g226)
    c: Coincident(g226,g227)
    c: Coincident(g228,g229)
    c: Coincident(g229,g230)
    c: Coincident(g233,g234)
    c: Coincident(g234,g235)
    c: Coincident(g236,g237)
    c: Coincident(g237,g238)
    c: Coincident(g240,g241)
    c: Coincident(g241,g242)
    c: Coincident(g242,g243)
    c: Coincident(g245,g246)
    c: Coincident(g246,g247)
    c: Coincident(g251,g252)
    c: Coincident(g253,g254)
    c: Coincident(g254,g255)
    c: Coincident(g257,g258)
    c: Coincident(g258,g259)
    c: Coincident(g259,g260)
    c: Coincident(g262,g263)
    c: Coincident(g263,g264)
    c: Coincident(g265,g266)
    c: Coincident(g267,g268)
    c: Coincident(g268,g269)
    c: Coincident(g271,g272)
    c: Coincident(g273,g274)
    c: Coincident(g274,g275)
    c: Coincident(g277,g278)
    c: Coincident(g278,g279)
    c: Coincident(g281,g282)
    c: Coincident(g282,g283)
    c: Coincident(g284,g285)
    c: Coincident(g289,g290)
    c: Coincident(g290,g291)
    c: Coincident(g293,g294)
    c: Coincident(g294,g295)
    c: Coincident(g297,g298)
    c: Coincident(g298,g299)
    c: Coincident(g300,g301)
    c: Coincident(g303,g304)
    c: Coincident(g305,g306)
    c: Coincident(g307,g308)
    c: Coincident(g308,g309)
    c: Coincident(g311,g312)
    c: Coincident(g312,g313)
    c: Coincident(g316,g317)
    c: Coincident(g319,g320)
    c: Coincident(g320,g321)
    c: Coincident(g322,g323)
    c: Coincident(g323,g324)
    c: Coincident(g327,g328)
    c: Coincident(g329,g330)
    c: Coincident(g330,g331)
    c: Coincident(g333,g334)
    c: Coincident(g334,g335)
    c: Coincident(g337,g338)
    c: Coincident(g339,g340)
    c: Coincident(g340,g341)
    c: Coincident(g343,g344)
    c: Coincident(g344,g345)
    c: Coincident(g348,g349)
    c: Coincident(g349,g350)
    c: Coincident(g351,g352)
    c: Coincident(g352,g353)
    c: Coincident(g356,g357)
    c: Coincident(g358,g359)
    c: Coincident(g359,g360)
    c: Coincident(g361,g362)
    c: Coincident(g362,g363)
    c: Coincident(g364,g365)
    c: Coincident(g365,g366)
    c: Coincident(g366,g367)
    c: Coincident(g370,g371)
    c: Coincident(g371,g372)
    c: Coincident(g373,g374)
    c: Coincident(g374,g375)
    c: Coincident(g377,g378)
    c: Coincident(g381,g382)
    c: Coincident(g382,g383)
    c: Coincident(g385,g386)
    c: Coincident(g386,g387)
    c: Coincident(g388,g389)
    c: Coincident(g392,g393)
    c: Coincident(g393,g394)
    c: Coincident(g396,g397)
    c: Coincident(g397,g398)
    c: Coincident(g400,g401)
    c: Coincident(g401,g402)
    c: Coincident(g403,g404)
    c: Coincident(g406,g407)
    c: Coincident(g408,g409)
    c: Coincident(g410,g411)
    c: Coincident(g411,g412)
    c: Coincident(g414,g415)
    c: Coincident(g415,g416)
    c: Coincident(g419,g420)
    c: Coincident(g423,g424)
    c: Coincident(g425,g426)
    c: Coincident(g426,g427)
    c: Coincident(g429,g430)
    c: Coincident(g430,g431)
    c: Coincident(g433,g434)
    c: Coincident(g434,g435)
    c: Coincident(g436,g437)
    c: Coincident(g437,g438)
    c: Coincident(g441,g442)
    c: Coincident(g443,g444)
    c: Coincident(g444,g445)
    c: Coincident(g447,g448)
    c: Coincident(g448,g449)
    c: Coincident(g451,g452)
    c: Coincident(g453,g454)
    c: Coincident(g457,g458)
    c: Coincident(g459,g460)
    c: Coincident(g460,g461)
    c: Coincident(g463,g464)
    c: Coincident(g464,g465)
    c: Coincident(g466,g467)
    c: Coincident(g467,g468)
    c: Coincident(g470,g471)
